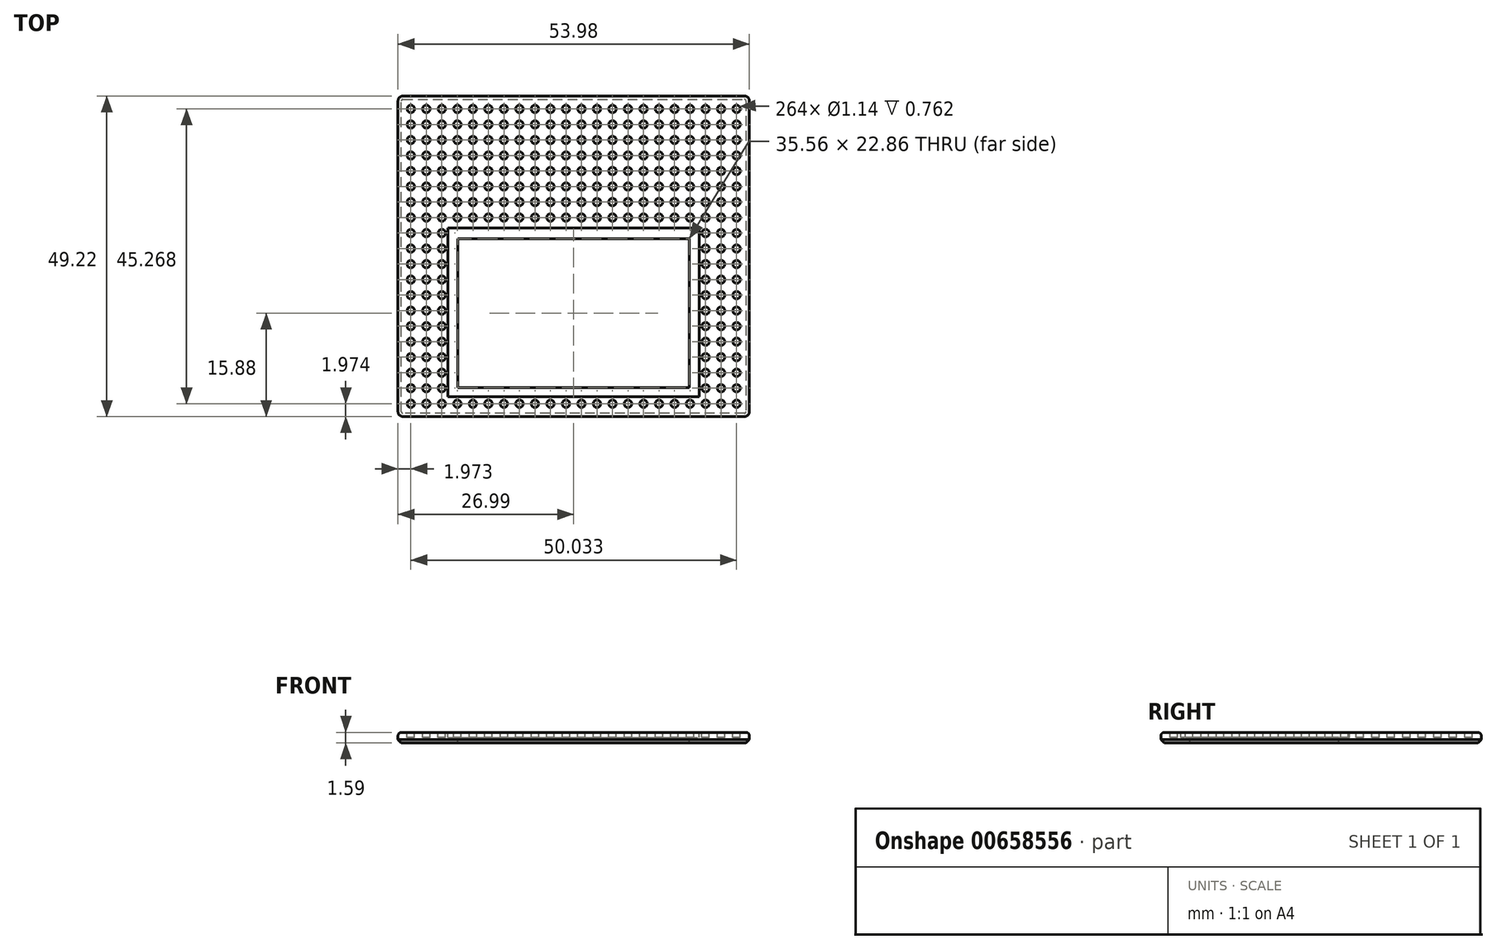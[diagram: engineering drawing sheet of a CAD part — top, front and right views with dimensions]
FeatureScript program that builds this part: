
annotation { "Feature Type Name" : "Feature", "Feature Type Description" : "" }
export const myFeature = defineFeature(function(context is Context, id is Id, definition is map)
    precondition{}
    {
        {
            var Q0;
            Q0=qCreatedBy(makeId("Top.planeOp"),FACE);
            var sketch = newSketch(context, id + "F0", { "sketchPlane" : qUnion([Q0])});
            skLineSegment(sketch, "E0.bottom", {"start": v(-26.99, 33.34) * mm, "end": v(26.99, 33.34) * mm});
            skLineSegment(sketch, "E0.top", {"start": v(-26.99, -15.88) * mm, "end": v(26.99, -15.88) * mm});
            skLineSegment(sketch, "E0.left", {"start": v(-26.99, 33.34) * mm, "end": v(-26.99, -15.88) * mm});
            skLineSegment(sketch, "E0.right", {"start": v(26.99, 33.34) * mm, "end": v(26.99, -15.87) * mm});
            skSolve(sketch);
        }
        {
            var Q0;
            Q0=qSketchRegion(id+"F0",true);
            extrude(context, id + "F1", {"entities" : qUnion([Q0]), "depth" : 1.59 * mm, "offsetDistance" : 25.4 * mm});
        }
        {
            var Q0;
            Q0=makeQuery(id+"F1.opExtrude","CAP_FACE",FACE,{"disambiguationData":[OSD([sQuery(id+"F0.wireOp",EDGE,"E0.bottom"),sQuery(id+"F0.wireOp",EDGE,"E0.top"),sQuery(id+"F0.wireOp",EDGE,"E0.left"),sQuery(id+"F0.wireOp",EDGE,"E0.right")])],"isStart":false});
            var sketch = newSketch(context, id + "F2", { "sketchPlane" : qUnion([Q0])});
            skCircle(sketch, "E1", {"center": v(-25.02, -13.9) * mm, "radius": 0.57 * mm});
            skCircle(sketch, "E2.0.1.0", {"center": v(-25.02, -11.52) * mm, "radius": 0.57 * mm});
            skCircle(sketch, "E2.0.2.0", {"center": v(-25.02, -9.14) * mm, "radius": 0.57 * mm});
            skCircle(sketch, "E2.0.3.0", {"center": v(-25.02, -6.76) * mm, "radius": 0.57 * mm});
            skCircle(sketch, "E2.0.4.0", {"center": v(-25.02, -4.38) * mm, "radius": 0.57 * mm});
            skCircle(sketch, "E2.0.5.0", {"center": v(-25.02, -2) * mm, "radius": 0.57 * mm});
            skCircle(sketch, "E2.0.6.0", {"center": v(-25.02, 0.39) * mm, "radius": 0.57 * mm});
            skCircle(sketch, "E2.0.7.0", {"center": v(-25.02, 2.77) * mm, "radius": 0.57 * mm});
            skCircle(sketch, "E2.0.8.0", {"center": v(-25.02, 5.15) * mm, "radius": 0.57 * mm});
            skCircle(sketch, "E2.0.9.0", {"center": v(-25.02, 7.54) * mm, "radius": 0.57 * mm});
            skCircle(sketch, "E2.0.10.0", {"center": v(-25.02, 9.92) * mm, "radius": 0.57 * mm});
            skCircle(sketch, "E2.0.11.0", {"center": v(-25.02, 12.3) * mm, "radius": 0.57 * mm});
            skCircle(sketch, "E2.1.0.0", {"center": v(-22.63, -13.9) * mm, "radius": 0.57 * mm});
            skCircle(sketch, "E2.1.1.0", {"center": v(-22.63, -11.52) * mm, "radius": 0.57 * mm});
            skCircle(sketch, "E2.1.2.0", {"center": v(-22.63, -9.14) * mm, "radius": 0.57 * mm});
            skCircle(sketch, "E2.1.3.0", {"center": v(-22.63, -6.76) * mm, "radius": 0.57 * mm});
            skCircle(sketch, "E2.1.4.0", {"center": v(-22.63, -4.38) * mm, "radius": 0.57 * mm});
            skCircle(sketch, "E2.1.5.0", {"center": v(-22.63, -2) * mm, "radius": 0.57 * mm});
            skCircle(sketch, "E2.1.6.0", {"center": v(-22.63, 0.39) * mm, "radius": 0.57 * mm});
            skCircle(sketch, "E2.1.7.0", {"center": v(-22.63, 2.77) * mm, "radius": 0.57 * mm});
            skCircle(sketch, "E2.1.8.0", {"center": v(-22.63, 5.15) * mm, "radius": 0.57 * mm});
            skCircle(sketch, "E2.1.9.0", {"center": v(-22.63, 7.54) * mm, "radius": 0.57 * mm});
            skCircle(sketch, "E2.1.10.0", {"center": v(-22.63, 9.92) * mm, "radius": 0.57 * mm});
            skCircle(sketch, "E2.1.11.0", {"center": v(-22.63, 12.3) * mm, "radius": 0.57 * mm});
            skCircle(sketch, "E2.2.0.0", {"center": v(-20.25, -13.9) * mm, "radius": 0.57 * mm});
            skCircle(sketch, "E2.2.1.0", {"center": v(-20.25, -11.52) * mm, "radius": 0.57 * mm});
            skCircle(sketch, "E2.2.2.0", {"center": v(-20.25, -9.14) * mm, "radius": 0.57 * mm});
            skCircle(sketch, "E2.2.3.0", {"center": v(-20.25, -6.76) * mm, "radius": 0.57 * mm});
            skCircle(sketch, "E2.2.4.0", {"center": v(-20.25, -4.38) * mm, "radius": 0.57 * mm});
            skCircle(sketch, "E2.2.5.0", {"center": v(-20.25, -2) * mm, "radius": 0.57 * mm});
            skCircle(sketch, "E2.2.6.0", {"center": v(-20.25, 0.39) * mm, "radius": 0.57 * mm});
            skCircle(sketch, "E2.2.7.0", {"center": v(-20.25, 2.77) * mm, "radius": 0.57 * mm});
            skCircle(sketch, "E2.2.8.0", {"center": v(-20.25, 5.15) * mm, "radius": 0.57 * mm});
            skCircle(sketch, "E2.2.9.0", {"center": v(-20.25, 7.54) * mm, "radius": 0.57 * mm});
            skCircle(sketch, "E2.2.10.0", {"center": v(-20.25, 9.92) * mm, "radius": 0.57 * mm});
            skCircle(sketch, "E2.2.11.0", {"center": v(-20.25, 12.3) * mm, "radius": 0.57 * mm});
            skCircle(sketch, "E2.3.0.0", {"center": v(-17.87, -13.9) * mm, "radius": 0.57 * mm});
            skCircle(sketch, "E2.3.1.0", {"center": v(-17.87, -11.52) * mm, "radius": 0.57 * mm});
            skCircle(sketch, "E2.3.2.0", {"center": v(-17.87, -9.14) * mm, "radius": 0.57 * mm});
            skCircle(sketch, "E2.3.3.0", {"center": v(-17.87, -6.76) * mm, "radius": 0.57 * mm});
            skCircle(sketch, "E2.3.4.0", {"center": v(-17.87, -4.38) * mm, "radius": 0.57 * mm});
            skCircle(sketch, "E2.3.5.0", {"center": v(-17.87, -2) * mm, "radius": 0.57 * mm});
            skCircle(sketch, "E2.3.6.0", {"center": v(-17.87, 0.39) * mm, "radius": 0.57 * mm});
            skCircle(sketch, "E2.3.7.0", {"center": v(-17.87, 2.77) * mm, "radius": 0.57 * mm});
            skCircle(sketch, "E2.3.8.0", {"center": v(-17.87, 5.15) * mm, "radius": 0.57 * mm});
            skCircle(sketch, "E2.3.9.0", {"center": v(-17.87, 7.54) * mm, "radius": 0.57 * mm});
            skCircle(sketch, "E2.3.10.0", {"center": v(-17.87, 9.92) * mm, "radius": 0.57 * mm});
            skCircle(sketch, "E2.3.11.0", {"center": v(-17.87, 12.3) * mm, "radius": 0.57 * mm});
            skCircle(sketch, "E2.4.0.0", {"center": v(-15.49, -13.9) * mm, "radius": 0.57 * mm});
            skCircle(sketch, "E2.4.1.0", {"center": v(-15.49, -11.52) * mm, "radius": 0.57 * mm});
            skCircle(sketch, "E2.4.2.0", {"center": v(-15.49, -9.14) * mm, "radius": 0.57 * mm});
            skCircle(sketch, "E2.4.3.0", {"center": v(-15.49, -6.76) * mm, "radius": 0.57 * mm});
            skCircle(sketch, "E2.4.4.0", {"center": v(-15.49, -4.38) * mm, "radius": 0.57 * mm});
            skCircle(sketch, "E2.4.5.0", {"center": v(-15.49, -2) * mm, "radius": 0.57 * mm});
            skCircle(sketch, "E2.4.6.0", {"center": v(-15.49, 0.39) * mm, "radius": 0.57 * mm});
            skCircle(sketch, "E2.4.7.0", {"center": v(-15.49, 2.77) * mm, "radius": 0.57 * mm});
            skCircle(sketch, "E2.4.8.0", {"center": v(-15.49, 5.15) * mm, "radius": 0.57 * mm});
            skCircle(sketch, "E2.4.9.0", {"center": v(-15.49, 7.54) * mm, "radius": 0.57 * mm});
            skCircle(sketch, "E2.4.10.0", {"center": v(-15.49, 9.92) * mm, "radius": 0.57 * mm});
            skCircle(sketch, "E2.4.11.0", {"center": v(-15.49, 12.3) * mm, "radius": 0.57 * mm});
            skCircle(sketch, "E2.5.0.0", {"center": v(-13.1, -13.9) * mm, "radius": 0.57 * mm});
            skCircle(sketch, "E2.5.1.0", {"center": v(-13.1, -11.52) * mm, "radius": 0.57 * mm});
            skCircle(sketch, "E2.5.2.0", {"center": v(-13.1, -9.14) * mm, "radius": 0.57 * mm});
            skCircle(sketch, "E2.5.3.0", {"center": v(-13.1, -6.76) * mm, "radius": 0.57 * mm});
            skCircle(sketch, "E2.5.4.0", {"center": v(-13.1, -4.38) * mm, "radius": 0.57 * mm});
            skCircle(sketch, "E2.5.5.0", {"center": v(-13.1, -2) * mm, "radius": 0.57 * mm});
            skCircle(sketch, "E2.5.6.0", {"center": v(-13.1, 0.39) * mm, "radius": 0.57 * mm});
            skCircle(sketch, "E2.5.7.0", {"center": v(-13.1, 2.77) * mm, "radius": 0.57 * mm});
            skCircle(sketch, "E2.5.8.0", {"center": v(-13.1, 5.15) * mm, "radius": 0.57 * mm});
            skCircle(sketch, "E2.5.9.0", {"center": v(-13.1, 7.54) * mm, "radius": 0.57 * mm});
            skCircle(sketch, "E2.5.10.0", {"center": v(-13.1, 9.92) * mm, "radius": 0.57 * mm});
            skCircle(sketch, "E2.5.11.0", {"center": v(-13.1, 12.3) * mm, "radius": 0.57 * mm});
            skCircle(sketch, "E2.6.0.0", {"center": v(-10.72, -13.9) * mm, "radius": 0.57 * mm});
            skCircle(sketch, "E2.6.1.0", {"center": v(-10.72, -11.52) * mm, "radius": 0.57 * mm});
            skCircle(sketch, "E2.6.2.0", {"center": v(-10.72, -9.14) * mm, "radius": 0.57 * mm});
            skCircle(sketch, "E2.6.3.0", {"center": v(-10.72, -6.76) * mm, "radius": 0.57 * mm});
            skCircle(sketch, "E2.6.4.0", {"center": v(-10.72, -4.38) * mm, "radius": 0.57 * mm});
            skCircle(sketch, "E2.6.5.0", {"center": v(-10.72, -2) * mm, "radius": 0.57 * mm});
            skCircle(sketch, "E2.6.6.0", {"center": v(-10.72, 0.39) * mm, "radius": 0.57 * mm});
            skCircle(sketch, "E2.6.7.0", {"center": v(-10.72, 2.77) * mm, "radius": 0.57 * mm});
            skCircle(sketch, "E2.6.8.0", {"center": v(-10.72, 5.15) * mm, "radius": 0.57 * mm});
            skCircle(sketch, "E2.6.9.0", {"center": v(-10.72, 7.54) * mm, "radius": 0.57 * mm});
            skCircle(sketch, "E2.6.10.0", {"center": v(-10.72, 9.92) * mm, "radius": 0.57 * mm});
            skCircle(sketch, "E2.6.11.0", {"center": v(-10.72, 12.3) * mm, "radius": 0.57 * mm});
            skCircle(sketch, "E2.7.0.0", {"center": v(-8.34, -13.9) * mm, "radius": 0.57 * mm});
            skCircle(sketch, "E2.7.1.0", {"center": v(-8.34, -11.52) * mm, "radius": 0.57 * mm});
            skCircle(sketch, "E2.7.2.0", {"center": v(-8.34, -9.14) * mm, "radius": 0.57 * mm});
            skCircle(sketch, "E2.7.3.0", {"center": v(-8.34, -6.76) * mm, "radius": 0.57 * mm});
            skCircle(sketch, "E2.7.4.0", {"center": v(-8.34, -4.38) * mm, "radius": 0.57 * mm});
            skCircle(sketch, "E2.7.5.0", {"center": v(-8.34, -2) * mm, "radius": 0.57 * mm});
            skCircle(sketch, "E2.7.6.0", {"center": v(-8.34, 0.39) * mm, "radius": 0.57 * mm});
            skCircle(sketch, "E2.7.7.0", {"center": v(-8.34, 2.77) * mm, "radius": 0.57 * mm});
            skCircle(sketch, "E2.7.8.0", {"center": v(-8.34, 5.15) * mm, "radius": 0.57 * mm});
            skCircle(sketch, "E2.7.9.0", {"center": v(-8.34, 7.54) * mm, "radius": 0.57 * mm});
            skCircle(sketch, "E2.7.10.0", {"center": v(-8.34, 9.92) * mm, "radius": 0.57 * mm});
            skCircle(sketch, "E2.7.11.0", {"center": v(-8.34, 12.3) * mm, "radius": 0.57 * mm});
            skCircle(sketch, "E2.8.0.0", {"center": v(-5.96, -13.9) * mm, "radius": 0.57 * mm});
            skCircle(sketch, "E2.8.1.0", {"center": v(-5.96, -11.52) * mm, "radius": 0.57 * mm});
            skCircle(sketch, "E2.8.2.0", {"center": v(-5.96, -9.14) * mm, "radius": 0.57 * mm});
            skCircle(sketch, "E2.8.3.0", {"center": v(-5.96, -6.76) * mm, "radius": 0.57 * mm});
            skCircle(sketch, "E2.8.4.0", {"center": v(-5.96, -4.38) * mm, "radius": 0.57 * mm});
            skCircle(sketch, "E2.8.5.0", {"center": v(-5.96, -2) * mm, "radius": 0.57 * mm});
            skCircle(sketch, "E2.8.6.0", {"center": v(-5.96, 0.39) * mm, "radius": 0.57 * mm});
            skCircle(sketch, "E2.8.7.0", {"center": v(-5.96, 2.77) * mm, "radius": 0.57 * mm});
            skCircle(sketch, "E2.8.8.0", {"center": v(-5.96, 5.15) * mm, "radius": 0.57 * mm});
            skCircle(sketch, "E2.8.9.0", {"center": v(-5.96, 7.54) * mm, "radius": 0.57 * mm});
            skCircle(sketch, "E2.8.10.0", {"center": v(-5.96, 9.92) * mm, "radius": 0.57 * mm});
            skCircle(sketch, "E2.8.11.0", {"center": v(-5.96, 12.3) * mm, "radius": 0.57 * mm});
            skCircle(sketch, "E2.9.0.0", {"center": v(-3.57, -13.9) * mm, "radius": 0.57 * mm});
            skCircle(sketch, "E2.9.1.0", {"center": v(-3.57, -11.52) * mm, "radius": 0.57 * mm});
            skCircle(sketch, "E2.9.2.0", {"center": v(-3.57, -9.14) * mm, "radius": 0.57 * mm});
            skCircle(sketch, "E2.9.3.0", {"center": v(-3.57, -6.76) * mm, "radius": 0.57 * mm});
            skCircle(sketch, "E2.9.4.0", {"center": v(-3.57, -4.38) * mm, "radius": 0.57 * mm});
            skCircle(sketch, "E2.9.5.0", {"center": v(-3.57, -2) * mm, "radius": 0.57 * mm});
            skCircle(sketch, "E2.9.6.0", {"center": v(-3.57, 0.39) * mm, "radius": 0.57 * mm});
            skCircle(sketch, "E2.9.7.0", {"center": v(-3.57, 2.77) * mm, "radius": 0.57 * mm});
            skCircle(sketch, "E2.9.8.0", {"center": v(-3.57, 5.15) * mm, "radius": 0.57 * mm});
            skCircle(sketch, "E2.9.9.0", {"center": v(-3.57, 7.54) * mm, "radius": 0.57 * mm});
            skCircle(sketch, "E2.9.10.0", {"center": v(-3.57, 9.92) * mm, "radius": 0.57 * mm});
            skCircle(sketch, "E2.9.11.0", {"center": v(-3.57, 12.3) * mm, "radius": 0.57 * mm});
            skCircle(sketch, "E2.10.0.0", {"center": v(-1.2, -13.9) * mm, "radius": 0.57 * mm});
            skCircle(sketch, "E2.10.1.0", {"center": v(-1.2, -11.52) * mm, "radius": 0.57 * mm});
            skCircle(sketch, "E2.10.2.0", {"center": v(-1.2, -9.14) * mm, "radius": 0.57 * mm});
            skCircle(sketch, "E2.10.3.0", {"center": v(-1.2, -6.76) * mm, "radius": 0.57 * mm});
            skCircle(sketch, "E2.10.4.0", {"center": v(-1.2, -4.38) * mm, "radius": 0.57 * mm});
            skCircle(sketch, "E2.10.5.0", {"center": v(-1.2, -2) * mm, "radius": 0.57 * mm});
            skCircle(sketch, "E2.10.6.0", {"center": v(-1.2, 0.39) * mm, "radius": 0.57 * mm});
            skCircle(sketch, "E2.10.7.0", {"center": v(-1.2, 2.77) * mm, "radius": 0.57 * mm});
            skCircle(sketch, "E2.10.8.0", {"center": v(-1.2, 5.15) * mm, "radius": 0.57 * mm});
            skCircle(sketch, "E2.10.9.0", {"center": v(-1.2, 7.54) * mm, "radius": 0.57 * mm});
            skCircle(sketch, "E2.10.10.0", {"center": v(-1.2, 9.92) * mm, "radius": 0.57 * mm});
            skCircle(sketch, "E2.10.11.0", {"center": v(-1.2, 12.3) * mm, "radius": 0.57 * mm});
            skCircle(sketch, "E2.11.0.0", {"center": v(1.2, -13.9) * mm, "radius": 0.57 * mm});
            skCircle(sketch, "E2.11.1.0", {"center": v(1.2, -11.52) * mm, "radius": 0.57 * mm});
            skCircle(sketch, "E2.11.2.0", {"center": v(1.2, -9.14) * mm, "radius": 0.57 * mm});
            skCircle(sketch, "E2.11.3.0", {"center": v(1.2, -6.76) * mm, "radius": 0.57 * mm});
            skCircle(sketch, "E2.11.4.0", {"center": v(1.2, -4.38) * mm, "radius": 0.57 * mm});
            skCircle(sketch, "E2.11.5.0", {"center": v(1.2, -2) * mm, "radius": 0.57 * mm});
            skCircle(sketch, "E2.11.6.0", {"center": v(1.2, 0.39) * mm, "radius": 0.57 * mm});
            skCircle(sketch, "E2.11.7.0", {"center": v(1.2, 2.77) * mm, "radius": 0.57 * mm});
            skCircle(sketch, "E2.11.8.0", {"center": v(1.2, 5.15) * mm, "radius": 0.57 * mm});
            skCircle(sketch, "E2.11.9.0", {"center": v(1.2, 7.54) * mm, "radius": 0.57 * mm});
            skCircle(sketch, "E2.11.10.0", {"center": v(1.2, 9.92) * mm, "radius": 0.57 * mm});
            skCircle(sketch, "E2.11.11.0", {"center": v(1.2, 12.3) * mm, "radius": 0.57 * mm});
            skCircle(sketch, "E2.12.0.0", {"center": v(3.57, -13.9) * mm, "radius": 0.57 * mm});
            skCircle(sketch, "E2.12.1.0", {"center": v(3.57, -11.52) * mm, "radius": 0.57 * mm});
            skCircle(sketch, "E2.12.2.0", {"center": v(3.57, -9.14) * mm, "radius": 0.57 * mm});
            skCircle(sketch, "E2.12.3.0", {"center": v(3.57, -6.76) * mm, "radius": 0.57 * mm});
            skCircle(sketch, "E2.12.4.0", {"center": v(3.57, -4.38) * mm, "radius": 0.57 * mm});
            skCircle(sketch, "E2.12.5.0", {"center": v(3.57, -2) * mm, "radius": 0.57 * mm});
            skCircle(sketch, "E2.12.6.0", {"center": v(3.57, 0.39) * mm, "radius": 0.57 * mm});
            skCircle(sketch, "E2.12.7.0", {"center": v(3.57, 2.77) * mm, "radius": 0.57 * mm});
            skCircle(sketch, "E2.12.8.0", {"center": v(3.57, 5.15) * mm, "radius": 0.57 * mm});
            skCircle(sketch, "E2.12.9.0", {"center": v(3.57, 7.54) * mm, "radius": 0.57 * mm});
            skCircle(sketch, "E2.12.10.0", {"center": v(3.57, 9.92) * mm, "radius": 0.57 * mm});
            skCircle(sketch, "E2.12.11.0", {"center": v(3.57, 12.3) * mm, "radius": 0.57 * mm});
            skCircle(sketch, "E2.13.0.0", {"center": v(5.96, -13.9) * mm, "radius": 0.57 * mm});
            skCircle(sketch, "E2.13.1.0", {"center": v(5.96, -11.52) * mm, "radius": 0.57 * mm});
            skCircle(sketch, "E2.13.2.0", {"center": v(5.96, -9.14) * mm, "radius": 0.57 * mm});
            skCircle(sketch, "E2.13.3.0", {"center": v(5.96, -6.76) * mm, "radius": 0.57 * mm});
            skCircle(sketch, "E2.13.4.0", {"center": v(5.96, -4.38) * mm, "radius": 0.57 * mm});
            skCircle(sketch, "E2.13.5.0", {"center": v(5.96, -2) * mm, "radius": 0.57 * mm});
            skCircle(sketch, "E2.13.6.0", {"center": v(5.96, 0.39) * mm, "radius": 0.57 * mm});
            skCircle(sketch, "E2.13.7.0", {"center": v(5.96, 2.77) * mm, "radius": 0.57 * mm});
            skCircle(sketch, "E2.13.8.0", {"center": v(5.96, 5.15) * mm, "radius": 0.57 * mm});
            skCircle(sketch, "E2.13.9.0", {"center": v(5.96, 7.54) * mm, "radius": 0.57 * mm});
            skCircle(sketch, "E2.13.10.0", {"center": v(5.96, 9.92) * mm, "radius": 0.57 * mm});
            skCircle(sketch, "E2.13.11.0", {"center": v(5.96, 12.3) * mm, "radius": 0.57 * mm});
            skCircle(sketch, "E2.14.0.0", {"center": v(8.34, -13.9) * mm, "radius": 0.57 * mm});
            skCircle(sketch, "E2.14.1.0", {"center": v(8.34, -11.52) * mm, "radius": 0.57 * mm});
            skCircle(sketch, "E2.14.2.0", {"center": v(8.34, -9.14) * mm, "radius": 0.57 * mm});
            skCircle(sketch, "E2.14.3.0", {"center": v(8.34, -6.76) * mm, "radius": 0.57 * mm});
            skCircle(sketch, "E2.14.4.0", {"center": v(8.34, -4.38) * mm, "radius": 0.57 * mm});
            skCircle(sketch, "E2.14.5.0", {"center": v(8.34, -2) * mm, "radius": 0.57 * mm});
            skCircle(sketch, "E2.14.6.0", {"center": v(8.34, 0.39) * mm, "radius": 0.57 * mm});
            skCircle(sketch, "E2.14.7.0", {"center": v(8.34, 2.77) * mm, "radius": 0.57 * mm});
            skCircle(sketch, "E2.14.8.0", {"center": v(8.34, 5.15) * mm, "radius": 0.57 * mm});
            skCircle(sketch, "E2.14.9.0", {"center": v(8.34, 7.54) * mm, "radius": 0.57 * mm});
            skCircle(sketch, "E2.14.10.0", {"center": v(8.34, 9.92) * mm, "radius": 0.57 * mm});
            skCircle(sketch, "E2.14.11.0", {"center": v(8.34, 12.3) * mm, "radius": 0.57 * mm});
            skCircle(sketch, "E2.15.0.0", {"center": v(10.72, -13.9) * mm, "radius": 0.57 * mm});
            skCircle(sketch, "E2.15.1.0", {"center": v(10.72, -11.52) * mm, "radius": 0.57 * mm});
            skCircle(sketch, "E2.15.2.0", {"center": v(10.72, -9.14) * mm, "radius": 0.57 * mm});
            skCircle(sketch, "E2.15.3.0", {"center": v(10.72, -6.76) * mm, "radius": 0.57 * mm});
            skCircle(sketch, "E2.15.4.0", {"center": v(10.72, -4.38) * mm, "radius": 0.57 * mm});
            skCircle(sketch, "E2.15.5.0", {"center": v(10.72, -2) * mm, "radius": 0.57 * mm});
            skCircle(sketch, "E2.15.6.0", {"center": v(10.72, 0.39) * mm, "radius": 0.57 * mm});
            skCircle(sketch, "E2.15.7.0", {"center": v(10.72, 2.77) * mm, "radius": 0.57 * mm});
            skCircle(sketch, "E2.15.8.0", {"center": v(10.72, 5.15) * mm, "radius": 0.57 * mm});
            skCircle(sketch, "E2.15.9.0", {"center": v(10.72, 7.54) * mm, "radius": 0.57 * mm});
            skCircle(sketch, "E2.15.10.0", {"center": v(10.72, 9.92) * mm, "radius": 0.57 * mm});
            skCircle(sketch, "E2.15.11.0", {"center": v(10.72, 12.3) * mm, "radius": 0.57 * mm});
            skCircle(sketch, "E2.16.0.0", {"center": v(13.1, -13.9) * mm, "radius": 0.57 * mm});
            skCircle(sketch, "E2.16.1.0", {"center": v(13.1, -11.52) * mm, "radius": 0.57 * mm});
            skCircle(sketch, "E2.16.2.0", {"center": v(13.1, -9.14) * mm, "radius": 0.57 * mm});
            skCircle(sketch, "E2.16.3.0", {"center": v(13.1, -6.76) * mm, "radius": 0.57 * mm});
            skCircle(sketch, "E2.16.4.0", {"center": v(13.1, -4.38) * mm, "radius": 0.57 * mm});
            skCircle(sketch, "E2.16.5.0", {"center": v(13.1, -2) * mm, "radius": 0.57 * mm});
            skCircle(sketch, "E2.16.6.0", {"center": v(13.1, 0.39) * mm, "radius": 0.57 * mm});
            skCircle(sketch, "E2.16.7.0", {"center": v(13.1, 2.77) * mm, "radius": 0.57 * mm});
            skCircle(sketch, "E2.16.8.0", {"center": v(13.1, 5.15) * mm, "radius": 0.57 * mm});
            skCircle(sketch, "E2.16.9.0", {"center": v(13.1, 7.54) * mm, "radius": 0.57 * mm});
            skCircle(sketch, "E2.16.10.0", {"center": v(13.1, 9.92) * mm, "radius": 0.57 * mm});
            skCircle(sketch, "E2.16.11.0", {"center": v(13.1, 12.3) * mm, "radius": 0.57 * mm});
            skCircle(sketch, "E2.17.0.0", {"center": v(15.49, -13.9) * mm, "radius": 0.57 * mm});
            skCircle(sketch, "E2.17.1.0", {"center": v(15.49, -11.52) * mm, "radius": 0.57 * mm});
            skCircle(sketch, "E2.17.2.0", {"center": v(15.49, -9.14) * mm, "radius": 0.57 * mm});
            skCircle(sketch, "E2.17.3.0", {"center": v(15.49, -6.76) * mm, "radius": 0.57 * mm});
            skCircle(sketch, "E2.17.4.0", {"center": v(15.49, -4.38) * mm, "radius": 0.57 * mm});
            skCircle(sketch, "E2.17.5.0", {"center": v(15.49, -2) * mm, "radius": 0.57 * mm});
            skCircle(sketch, "E2.17.6.0", {"center": v(15.49, 0.39) * mm, "radius": 0.57 * mm});
            skCircle(sketch, "E2.17.7.0", {"center": v(15.49, 2.77) * mm, "radius": 0.57 * mm});
            skCircle(sketch, "E2.17.8.0", {"center": v(15.49, 5.15) * mm, "radius": 0.57 * mm});
            skCircle(sketch, "E2.17.9.0", {"center": v(15.49, 7.54) * mm, "radius": 0.57 * mm});
            skCircle(sketch, "E2.17.10.0", {"center": v(15.49, 9.92) * mm, "radius": 0.57 * mm});
            skCircle(sketch, "E2.17.11.0", {"center": v(15.49, 12.3) * mm, "radius": 0.57 * mm});
            skCircle(sketch, "E2.18.0.0", {"center": v(17.87, -13.9) * mm, "radius": 0.57 * mm});
            skCircle(sketch, "E2.18.1.0", {"center": v(17.87, -11.52) * mm, "radius": 0.57 * mm});
            skCircle(sketch, "E2.18.2.0", {"center": v(17.87, -9.14) * mm, "radius": 0.57 * mm});
            skCircle(sketch, "E2.18.3.0", {"center": v(17.87, -6.76) * mm, "radius": 0.57 * mm});
            skCircle(sketch, "E2.18.4.0", {"center": v(17.87, -4.38) * mm, "radius": 0.57 * mm});
            skCircle(sketch, "E2.18.5.0", {"center": v(17.87, -2) * mm, "radius": 0.57 * mm});
            skCircle(sketch, "E2.18.6.0", {"center": v(17.87, 0.39) * mm, "radius": 0.57 * mm});
            skCircle(sketch, "E2.18.7.0", {"center": v(17.87, 2.77) * mm, "radius": 0.57 * mm});
            skCircle(sketch, "E2.18.8.0", {"center": v(17.87, 5.15) * mm, "radius": 0.57 * mm});
            skCircle(sketch, "E2.18.9.0", {"center": v(17.87, 7.54) * mm, "radius": 0.57 * mm});
            skCircle(sketch, "E2.18.10.0", {"center": v(17.87, 9.92) * mm, "radius": 0.57 * mm});
            skCircle(sketch, "E2.18.11.0", {"center": v(17.87, 12.3) * mm, "radius": 0.57 * mm});
            skCircle(sketch, "E2.19.0.0", {"center": v(20.25, -13.9) * mm, "radius": 0.57 * mm});
            skCircle(sketch, "E2.19.1.0", {"center": v(20.25, -11.52) * mm, "radius": 0.57 * mm});
            skCircle(sketch, "E2.19.2.0", {"center": v(20.25, -9.14) * mm, "radius": 0.57 * mm});
            skCircle(sketch, "E2.19.3.0", {"center": v(20.25, -6.76) * mm, "radius": 0.57 * mm});
            skCircle(sketch, "E2.19.4.0", {"center": v(20.25, -4.38) * mm, "radius": 0.57 * mm});
            skCircle(sketch, "E2.19.5.0", {"center": v(20.25, -2) * mm, "radius": 0.57 * mm});
            skCircle(sketch, "E2.19.6.0", {"center": v(20.25, 0.39) * mm, "radius": 0.57 * mm});
            skCircle(sketch, "E2.19.7.0", {"center": v(20.25, 2.77) * mm, "radius": 0.57 * mm});
            skCircle(sketch, "E2.19.8.0", {"center": v(20.25, 5.15) * mm, "radius": 0.57 * mm});
            skCircle(sketch, "E2.19.9.0", {"center": v(20.25, 7.54) * mm, "radius": 0.57 * mm});
            skCircle(sketch, "E2.19.10.0", {"center": v(20.25, 9.92) * mm, "radius": 0.57 * mm});
            skCircle(sketch, "E2.19.11.0", {"center": v(20.25, 12.3) * mm, "radius": 0.57 * mm});
            skCircle(sketch, "E2.20.0.0", {"center": v(22.63, -13.9) * mm, "radius": 0.57 * mm});
            skCircle(sketch, "E2.20.1.0", {"center": v(22.63, -11.52) * mm, "radius": 0.57 * mm});
            skCircle(sketch, "E2.20.2.0", {"center": v(22.63, -9.14) * mm, "radius": 0.57 * mm});
            skCircle(sketch, "E2.20.3.0", {"center": v(22.63, -6.76) * mm, "radius": 0.57 * mm});
            skCircle(sketch, "E2.20.4.0", {"center": v(22.63, -4.38) * mm, "radius": 0.57 * mm});
            skCircle(sketch, "E2.20.5.0", {"center": v(22.63, -2) * mm, "radius": 0.57 * mm});
            skCircle(sketch, "E2.20.6.0", {"center": v(22.63, 0.39) * mm, "radius": 0.57 * mm});
            skCircle(sketch, "E2.20.7.0", {"center": v(22.63, 2.77) * mm, "radius": 0.57 * mm});
            skCircle(sketch, "E2.20.8.0", {"center": v(22.63, 5.15) * mm, "radius": 0.57 * mm});
            skCircle(sketch, "E2.20.9.0", {"center": v(22.63, 7.54) * mm, "radius": 0.57 * mm});
            skCircle(sketch, "E2.20.10.0", {"center": v(22.63, 9.92) * mm, "radius": 0.57 * mm});
            skCircle(sketch, "E2.20.11.0", {"center": v(22.63, 12.3) * mm, "radius": 0.57 * mm});
            skCircle(sketch, "E2.21.0.0", {"center": v(25.02, -13.9) * mm, "radius": 0.57 * mm});
            skCircle(sketch, "E2.21.1.0", {"center": v(25.02, -11.52) * mm, "radius": 0.57 * mm});
            skCircle(sketch, "E2.21.2.0", {"center": v(25.02, -9.14) * mm, "radius": 0.57 * mm});
            skCircle(sketch, "E2.21.3.0", {"center": v(25.02, -6.76) * mm, "radius": 0.57 * mm});
            skCircle(sketch, "E2.21.4.0", {"center": v(25.02, -4.38) * mm, "radius": 0.57 * mm});
            skCircle(sketch, "E2.21.5.0", {"center": v(25.02, -2) * mm, "radius": 0.57 * mm});
            skCircle(sketch, "E2.21.6.0", {"center": v(25.02, 0.39) * mm, "radius": 0.57 * mm});
            skCircle(sketch, "E2.21.7.0", {"center": v(25.02, 2.77) * mm, "radius": 0.57 * mm});
            skCircle(sketch, "E2.21.8.0", {"center": v(25.02, 5.15) * mm, "radius": 0.57 * mm});
            skCircle(sketch, "E2.21.9.0", {"center": v(25.02, 7.54) * mm, "radius": 0.57 * mm});
            skCircle(sketch, "E2.21.10.0", {"center": v(25.02, 9.92) * mm, "radius": 0.57 * mm});
            skCircle(sketch, "E2.21.11.0", {"center": v(25.02, 12.3) * mm, "radius": 0.57 * mm});
            skLineSegment(sketch, "E2.direction1", {"start": v(-25.02, -13.9) * mm, "end": v(-22.63, -13.9) * mm, "construction": true});
            skLineSegment(sketch, "E2.direction2", {"start": v(-25.02, -13.9) * mm, "end": v(-25.02, -11.52) * mm, "construction": true});
            skCircle(sketch, "E3.0.0.12", {"center": v(-25.02, 14.68) * mm, "radius": 0.57 * mm});
            skCircle(sketch, "E3.0.0.13", {"center": v(-25.02, 17.07) * mm, "radius": 0.57 * mm});
            skCircle(sketch, "E3.0.0.14", {"center": v(-25.02, 19.45) * mm, "radius": 0.57 * mm});
            skCircle(sketch, "E3.0.0.15", {"center": v(-25.02, 21.83) * mm, "radius": 0.57 * mm});
            skCircle(sketch, "E3.0.0.16", {"center": v(-25.02, 24.21) * mm, "radius": 0.57 * mm});
            skCircle(sketch, "E3.0.0.17", {"center": v(-25.02, 26.6) * mm, "radius": 0.57 * mm});
            skCircle(sketch, "E3.0.1.12", {"center": v(-22.63, 14.68) * mm, "radius": 0.57 * mm});
            skCircle(sketch, "E3.0.1.13", {"center": v(-22.63, 17.07) * mm, "radius": 0.57 * mm});
            skCircle(sketch, "E3.0.1.14", {"center": v(-22.63, 19.45) * mm, "radius": 0.57 * mm});
            skCircle(sketch, "E3.0.1.15", {"center": v(-22.63, 21.83) * mm, "radius": 0.57 * mm});
            skCircle(sketch, "E3.0.1.16", {"center": v(-22.63, 24.21) * mm, "radius": 0.57 * mm});
            skCircle(sketch, "E3.0.1.17", {"center": v(-22.63, 26.6) * mm, "radius": 0.57 * mm});
            skCircle(sketch, "E3.0.2.12", {"center": v(-20.25, 14.68) * mm, "radius": 0.57 * mm});
            skCircle(sketch, "E3.0.2.13", {"center": v(-20.25, 17.07) * mm, "radius": 0.57 * mm});
            skCircle(sketch, "E3.0.2.14", {"center": v(-20.25, 19.45) * mm, "radius": 0.57 * mm});
            skCircle(sketch, "E3.0.2.15", {"center": v(-20.25, 21.83) * mm, "radius": 0.57 * mm});
            skCircle(sketch, "E3.0.2.16", {"center": v(-20.25, 24.21) * mm, "radius": 0.57 * mm});
            skCircle(sketch, "E3.0.2.17", {"center": v(-20.25, 26.6) * mm, "radius": 0.57 * mm});
            skCircle(sketch, "E3.0.3.12", {"center": v(-17.87, 14.68) * mm, "radius": 0.57 * mm});
            skCircle(sketch, "E3.0.3.13", {"center": v(-17.87, 17.07) * mm, "radius": 0.57 * mm});
            skCircle(sketch, "E3.0.3.14", {"center": v(-17.87, 19.45) * mm, "radius": 0.57 * mm});
            skCircle(sketch, "E3.0.3.15", {"center": v(-17.87, 21.83) * mm, "radius": 0.57 * mm});
            skCircle(sketch, "E3.0.3.16", {"center": v(-17.87, 24.21) * mm, "radius": 0.57 * mm});
            skCircle(sketch, "E3.0.3.17", {"center": v(-17.87, 26.6) * mm, "radius": 0.57 * mm});
            skCircle(sketch, "E3.0.4.12", {"center": v(-15.49, 14.68) * mm, "radius": 0.57 * mm});
            skCircle(sketch, "E3.0.4.13", {"center": v(-15.49, 17.07) * mm, "radius": 0.57 * mm});
            skCircle(sketch, "E3.0.4.14", {"center": v(-15.49, 19.45) * mm, "radius": 0.57 * mm});
            skCircle(sketch, "E3.0.4.15", {"center": v(-15.49, 21.83) * mm, "radius": 0.57 * mm});
            skCircle(sketch, "E3.0.4.16", {"center": v(-15.49, 24.21) * mm, "radius": 0.57 * mm});
            skCircle(sketch, "E3.0.4.17", {"center": v(-15.49, 26.6) * mm, "radius": 0.57 * mm});
            skCircle(sketch, "E3.0.5.12", {"center": v(-13.1, 14.68) * mm, "radius": 0.57 * mm});
            skCircle(sketch, "E3.0.5.13", {"center": v(-13.1, 17.07) * mm, "radius": 0.57 * mm});
            skCircle(sketch, "E3.0.5.14", {"center": v(-13.1, 19.45) * mm, "radius": 0.57 * mm});
            skCircle(sketch, "E3.0.5.15", {"center": v(-13.1, 21.83) * mm, "radius": 0.57 * mm});
            skCircle(sketch, "E3.0.5.16", {"center": v(-13.1, 24.21) * mm, "radius": 0.57 * mm});
            skCircle(sketch, "E3.0.5.17", {"center": v(-13.1, 26.6) * mm, "radius": 0.57 * mm});
            skCircle(sketch, "E3.0.6.12", {"center": v(-10.72, 14.68) * mm, "radius": 0.57 * mm});
            skCircle(sketch, "E3.0.6.13", {"center": v(-10.72, 17.07) * mm, "radius": 0.57 * mm});
            skCircle(sketch, "E3.0.6.14", {"center": v(-10.72, 19.45) * mm, "radius": 0.57 * mm});
            skCircle(sketch, "E3.0.6.15", {"center": v(-10.72, 21.83) * mm, "radius": 0.57 * mm});
            skCircle(sketch, "E3.0.6.16", {"center": v(-10.72, 24.21) * mm, "radius": 0.57 * mm});
            skCircle(sketch, "E3.0.6.17", {"center": v(-10.72, 26.6) * mm, "radius": 0.57 * mm});
            skCircle(sketch, "E3.0.7.12", {"center": v(-8.34, 14.68) * mm, "radius": 0.57 * mm});
            skCircle(sketch, "E3.0.7.13", {"center": v(-8.34, 17.07) * mm, "radius": 0.57 * mm});
            skCircle(sketch, "E3.0.7.14", {"center": v(-8.34, 19.45) * mm, "radius": 0.57 * mm});
            skCircle(sketch, "E3.0.7.15", {"center": v(-8.34, 21.83) * mm, "radius": 0.57 * mm});
            skCircle(sketch, "E3.0.7.16", {"center": v(-8.34, 24.21) * mm, "radius": 0.57 * mm});
            skCircle(sketch, "E3.0.7.17", {"center": v(-8.34, 26.6) * mm, "radius": 0.57 * mm});
            skCircle(sketch, "E3.0.8.12", {"center": v(-5.96, 14.68) * mm, "radius": 0.57 * mm});
            skCircle(sketch, "E3.0.8.13", {"center": v(-5.96, 17.07) * mm, "radius": 0.57 * mm});
            skCircle(sketch, "E3.0.8.14", {"center": v(-5.96, 19.45) * mm, "radius": 0.57 * mm});
            skCircle(sketch, "E3.0.8.15", {"center": v(-5.96, 21.83) * mm, "radius": 0.57 * mm});
            skCircle(sketch, "E3.0.8.16", {"center": v(-5.96, 24.21) * mm, "radius": 0.57 * mm});
            skCircle(sketch, "E3.0.8.17", {"center": v(-5.96, 26.6) * mm, "radius": 0.57 * mm});
            skCircle(sketch, "E3.0.9.12", {"center": v(-3.57, 14.68) * mm, "radius": 0.57 * mm});
            skCircle(sketch, "E3.0.9.13", {"center": v(-3.57, 17.07) * mm, "radius": 0.57 * mm});
            skCircle(sketch, "E3.0.9.14", {"center": v(-3.57, 19.45) * mm, "radius": 0.57 * mm});
            skCircle(sketch, "E3.0.9.15", {"center": v(-3.57, 21.83) * mm, "radius": 0.57 * mm});
            skCircle(sketch, "E3.0.9.16", {"center": v(-3.57, 24.21) * mm, "radius": 0.57 * mm});
            skCircle(sketch, "E3.0.9.17", {"center": v(-3.57, 26.6) * mm, "radius": 0.57 * mm});
            skCircle(sketch, "E3.0.10.12", {"center": v(-1.2, 14.68) * mm, "radius": 0.57 * mm});
            skCircle(sketch, "E3.0.10.13", {"center": v(-1.2, 17.07) * mm, "radius": 0.57 * mm});
            skCircle(sketch, "E3.0.10.14", {"center": v(-1.2, 19.45) * mm, "radius": 0.57 * mm});
            skCircle(sketch, "E3.0.10.15", {"center": v(-1.2, 21.83) * mm, "radius": 0.57 * mm});
            skCircle(sketch, "E3.0.10.16", {"center": v(-1.2, 24.21) * mm, "radius": 0.57 * mm});
            skCircle(sketch, "E3.0.10.17", {"center": v(-1.2, 26.6) * mm, "radius": 0.57 * mm});
            skCircle(sketch, "E3.0.11.12", {"center": v(1.2, 14.68) * mm, "radius": 0.57 * mm});
            skCircle(sketch, "E3.0.11.13", {"center": v(1.2, 17.07) * mm, "radius": 0.57 * mm});
            skCircle(sketch, "E3.0.11.14", {"center": v(1.2, 19.45) * mm, "radius": 0.57 * mm});
            skCircle(sketch, "E3.0.11.15", {"center": v(1.2, 21.83) * mm, "radius": 0.57 * mm});
            skCircle(sketch, "E3.0.11.16", {"center": v(1.2, 24.21) * mm, "radius": 0.57 * mm});
            skCircle(sketch, "E3.0.11.17", {"center": v(1.2, 26.6) * mm, "radius": 0.57 * mm});
            skCircle(sketch, "E3.0.12.12", {"center": v(3.57, 14.68) * mm, "radius": 0.57 * mm});
            skCircle(sketch, "E3.0.12.13", {"center": v(3.57, 17.07) * mm, "radius": 0.57 * mm});
            skCircle(sketch, "E3.0.12.14", {"center": v(3.57, 19.45) * mm, "radius": 0.57 * mm});
            skCircle(sketch, "E3.0.12.15", {"center": v(3.57, 21.83) * mm, "radius": 0.57 * mm});
            skCircle(sketch, "E3.0.12.16", {"center": v(3.57, 24.21) * mm, "radius": 0.57 * mm});
            skCircle(sketch, "E3.0.12.17", {"center": v(3.57, 26.6) * mm, "radius": 0.57 * mm});
            skCircle(sketch, "E3.0.13.12", {"center": v(5.96, 14.68) * mm, "radius": 0.57 * mm});
            skCircle(sketch, "E3.0.13.13", {"center": v(5.96, 17.07) * mm, "radius": 0.57 * mm});
            skCircle(sketch, "E3.0.13.14", {"center": v(5.96, 19.45) * mm, "radius": 0.57 * mm});
            skCircle(sketch, "E3.0.13.15", {"center": v(5.96, 21.83) * mm, "radius": 0.57 * mm});
            skCircle(sketch, "E3.0.13.16", {"center": v(5.96, 24.21) * mm, "radius": 0.57 * mm});
            skCircle(sketch, "E3.0.13.17", {"center": v(5.96, 26.6) * mm, "radius": 0.57 * mm});
            skCircle(sketch, "E3.0.14.12", {"center": v(8.34, 14.68) * mm, "radius": 0.57 * mm});
            skCircle(sketch, "E3.0.14.13", {"center": v(8.34, 17.07) * mm, "radius": 0.57 * mm});
            skCircle(sketch, "E3.0.14.14", {"center": v(8.34, 19.45) * mm, "radius": 0.57 * mm});
            skCircle(sketch, "E3.0.14.15", {"center": v(8.34, 21.83) * mm, "radius": 0.57 * mm});
            skCircle(sketch, "E3.0.14.16", {"center": v(8.34, 24.21) * mm, "radius": 0.57 * mm});
            skCircle(sketch, "E3.0.14.17", {"center": v(8.34, 26.6) * mm, "radius": 0.57 * mm});
            skCircle(sketch, "E3.0.15.12", {"center": v(10.72, 14.68) * mm, "radius": 0.57 * mm});
            skCircle(sketch, "E3.0.15.13", {"center": v(10.72, 17.07) * mm, "radius": 0.57 * mm});
            skCircle(sketch, "E3.0.15.14", {"center": v(10.72, 19.45) * mm, "radius": 0.57 * mm});
            skCircle(sketch, "E3.0.15.15", {"center": v(10.72, 21.83) * mm, "radius": 0.57 * mm});
            skCircle(sketch, "E3.0.15.16", {"center": v(10.72, 24.21) * mm, "radius": 0.57 * mm});
            skCircle(sketch, "E3.0.15.17", {"center": v(10.72, 26.6) * mm, "radius": 0.57 * mm});
            skCircle(sketch, "E3.0.16.12", {"center": v(13.1, 14.68) * mm, "radius": 0.57 * mm});
            skCircle(sketch, "E3.0.16.13", {"center": v(13.1, 17.07) * mm, "radius": 0.57 * mm});
            skCircle(sketch, "E3.0.16.14", {"center": v(13.1, 19.45) * mm, "radius": 0.57 * mm});
            skCircle(sketch, "E3.0.16.15", {"center": v(13.1, 21.83) * mm, "radius": 0.57 * mm});
            skCircle(sketch, "E3.0.16.16", {"center": v(13.1, 24.21) * mm, "radius": 0.57 * mm});
            skCircle(sketch, "E3.0.16.17", {"center": v(13.1, 26.6) * mm, "radius": 0.57 * mm});
            skCircle(sketch, "E3.0.17.12", {"center": v(15.49, 14.68) * mm, "radius": 0.57 * mm});
            skCircle(sketch, "E3.0.17.13", {"center": v(15.49, 17.07) * mm, "radius": 0.57 * mm});
            skCircle(sketch, "E3.0.17.14", {"center": v(15.49, 19.45) * mm, "radius": 0.57 * mm});
            skCircle(sketch, "E3.0.17.15", {"center": v(15.49, 21.83) * mm, "radius": 0.57 * mm});
            skCircle(sketch, "E3.0.17.16", {"center": v(15.49, 24.21) * mm, "radius": 0.57 * mm});
            skCircle(sketch, "E3.0.17.17", {"center": v(15.49, 26.6) * mm, "radius": 0.57 * mm});
            skCircle(sketch, "E3.0.18.12", {"center": v(17.87, 14.68) * mm, "radius": 0.57 * mm});
            skCircle(sketch, "E3.0.18.13", {"center": v(17.87, 17.07) * mm, "radius": 0.57 * mm});
            skCircle(sketch, "E3.0.18.14", {"center": v(17.87, 19.45) * mm, "radius": 0.57 * mm});
            skCircle(sketch, "E3.0.18.15", {"center": v(17.87, 21.83) * mm, "radius": 0.57 * mm});
            skCircle(sketch, "E3.0.18.16", {"center": v(17.87, 24.21) * mm, "radius": 0.57 * mm});
            skCircle(sketch, "E3.0.18.17", {"center": v(17.87, 26.6) * mm, "radius": 0.57 * mm});
            skCircle(sketch, "E3.0.19.12", {"center": v(20.25, 14.68) * mm, "radius": 0.57 * mm});
            skCircle(sketch, "E3.0.19.13", {"center": v(20.25, 17.07) * mm, "radius": 0.57 * mm});
            skCircle(sketch, "E3.0.19.14", {"center": v(20.25, 19.45) * mm, "radius": 0.57 * mm});
            skCircle(sketch, "E3.0.19.15", {"center": v(20.25, 21.83) * mm, "radius": 0.57 * mm});
            skCircle(sketch, "E3.0.19.16", {"center": v(20.25, 24.21) * mm, "radius": 0.57 * mm});
            skCircle(sketch, "E3.0.19.17", {"center": v(20.25, 26.6) * mm, "radius": 0.57 * mm});
            skCircle(sketch, "E3.0.20.12", {"center": v(22.63, 14.68) * mm, "radius": 0.57 * mm});
            skCircle(sketch, "E3.0.20.13", {"center": v(22.63, 17.07) * mm, "radius": 0.57 * mm});
            skCircle(sketch, "E3.0.20.14", {"center": v(22.63, 19.45) * mm, "radius": 0.57 * mm});
            skCircle(sketch, "E3.0.20.15", {"center": v(22.63, 21.83) * mm, "radius": 0.57 * mm});
            skCircle(sketch, "E3.0.20.16", {"center": v(22.63, 24.21) * mm, "radius": 0.57 * mm});
            skCircle(sketch, "E3.0.20.17", {"center": v(22.63, 26.6) * mm, "radius": 0.57 * mm});
            skCircle(sketch, "E3.0.21.12", {"center": v(25.02, 14.68) * mm, "radius": 0.57 * mm});
            skCircle(sketch, "E3.0.21.13", {"center": v(25.02, 17.07) * mm, "radius": 0.57 * mm});
            skCircle(sketch, "E3.0.21.14", {"center": v(25.02, 19.45) * mm, "radius": 0.57 * mm});
            skCircle(sketch, "E3.0.21.15", {"center": v(25.02, 21.83) * mm, "radius": 0.57 * mm});
            skCircle(sketch, "E3.0.21.16", {"center": v(25.02, 24.21) * mm, "radius": 0.57 * mm});
            skCircle(sketch, "E3.0.21.17", {"center": v(25.02, 26.6) * mm, "radius": 0.57 * mm});
            skCircle(sketch, "E4.0.0.18", {"center": v(-25.02, 28.98) * mm, "radius": 0.57 * mm});
            skCircle(sketch, "E4.0.1.18", {"center": v(-22.63, 28.98) * mm, "radius": 0.57 * mm});
            skCircle(sketch, "E4.0.2.18", {"center": v(-20.25, 28.98) * mm, "radius": 0.57 * mm});
            skCircle(sketch, "E4.0.3.18", {"center": v(-17.87, 28.98) * mm, "radius": 0.57 * mm});
            skCircle(sketch, "E4.0.4.18", {"center": v(-15.49, 28.98) * mm, "radius": 0.57 * mm});
            skCircle(sketch, "E4.0.5.18", {"center": v(-13.1, 28.98) * mm, "radius": 0.57 * mm});
            skCircle(sketch, "E4.0.6.18", {"center": v(-10.72, 28.98) * mm, "radius": 0.57 * mm});
            skCircle(sketch, "E4.0.7.18", {"center": v(-8.34, 28.98) * mm, "radius": 0.57 * mm});
            skCircle(sketch, "E4.0.8.18", {"center": v(-5.96, 28.98) * mm, "radius": 0.57 * mm});
            skCircle(sketch, "E4.0.9.18", {"center": v(-3.57, 28.98) * mm, "radius": 0.57 * mm});
            skCircle(sketch, "E4.0.10.18", {"center": v(-1.2, 28.98) * mm, "radius": 0.57 * mm});
            skCircle(sketch, "E4.0.11.18", {"center": v(1.2, 28.98) * mm, "radius": 0.57 * mm});
            skCircle(sketch, "E4.0.12.18", {"center": v(3.57, 28.98) * mm, "radius": 0.57 * mm});
            skCircle(sketch, "E4.0.13.18", {"center": v(5.96, 28.98) * mm, "radius": 0.57 * mm});
            skCircle(sketch, "E4.0.14.18", {"center": v(8.34, 28.98) * mm, "radius": 0.57 * mm});
            skCircle(sketch, "E4.0.15.18", {"center": v(10.72, 28.98) * mm, "radius": 0.57 * mm});
            skCircle(sketch, "E4.0.16.18", {"center": v(13.1, 28.98) * mm, "radius": 0.57 * mm});
            skCircle(sketch, "E4.0.17.18", {"center": v(15.49, 28.98) * mm, "radius": 0.57 * mm});
            skCircle(sketch, "E4.0.18.18", {"center": v(17.87, 28.98) * mm, "radius": 0.57 * mm});
            skCircle(sketch, "E4.0.19.18", {"center": v(20.25, 28.98) * mm, "radius": 0.57 * mm});
            skCircle(sketch, "E4.0.20.18", {"center": v(22.63, 28.98) * mm, "radius": 0.57 * mm});
            skCircle(sketch, "E4.0.21.18", {"center": v(25.02, 28.98) * mm, "radius": 0.57 * mm});
            skCircle(sketch, "E5.0.0.19", {"center": v(-25.02, 31.36) * mm, "radius": 0.57 * mm});
            skCircle(sketch, "E5.0.1.19", {"center": v(-22.63, 31.36) * mm, "radius": 0.57 * mm});
            skCircle(sketch, "E5.0.2.19", {"center": v(-20.25, 31.36) * mm, "radius": 0.57 * mm});
            skCircle(sketch, "E5.0.3.19", {"center": v(-17.87, 31.36) * mm, "radius": 0.57 * mm});
            skCircle(sketch, "E5.0.4.19", {"center": v(-15.49, 31.36) * mm, "radius": 0.57 * mm});
            skCircle(sketch, "E5.0.5.19", {"center": v(-13.1, 31.36) * mm, "radius": 0.57 * mm});
            skCircle(sketch, "E5.0.6.19", {"center": v(-10.72, 31.36) * mm, "radius": 0.57 * mm});
            skCircle(sketch, "E5.0.7.19", {"center": v(-8.34, 31.36) * mm, "radius": 0.57 * mm});
            skCircle(sketch, "E5.0.8.19", {"center": v(-5.96, 31.36) * mm, "radius": 0.57 * mm});
            skCircle(sketch, "E5.0.9.19", {"center": v(-3.57, 31.36) * mm, "radius": 0.57 * mm});
            skCircle(sketch, "E5.0.10.19", {"center": v(-1.2, 31.36) * mm, "radius": 0.57 * mm});
            skCircle(sketch, "E5.0.11.19", {"center": v(1.2, 31.36) * mm, "radius": 0.57 * mm});
            skCircle(sketch, "E5.0.12.19", {"center": v(3.57, 31.36) * mm, "radius": 0.57 * mm});
            skCircle(sketch, "E5.0.13.19", {"center": v(5.96, 31.36) * mm, "radius": 0.57 * mm});
            skCircle(sketch, "E5.0.14.19", {"center": v(8.34, 31.36) * mm, "radius": 0.57 * mm});
            skCircle(sketch, "E5.0.15.19", {"center": v(10.72, 31.36) * mm, "radius": 0.57 * mm});
            skCircle(sketch, "E5.0.16.19", {"center": v(13.1, 31.36) * mm, "radius": 0.57 * mm});
            skCircle(sketch, "E5.0.17.19", {"center": v(15.49, 31.36) * mm, "radius": 0.57 * mm});
            skCircle(sketch, "E5.0.18.19", {"center": v(17.87, 31.36) * mm, "radius": 0.57 * mm});
            skCircle(sketch, "E5.0.19.19", {"center": v(20.25, 31.36) * mm, "radius": 0.57 * mm});
            skCircle(sketch, "E5.0.20.19", {"center": v(22.63, 31.36) * mm, "radius": 0.57 * mm});
            skCircle(sketch, "E5.0.21.19", {"center": v(25.02, 31.36) * mm, "radius": 0.57 * mm});
            skSolve(sketch);
        }
        {
            var Q0;
            Q0=qSketchRegion(id+"F2",true);
            extrude(context, id + "F3", {"entities" : qUnion([Q0]), "operationType" : NewBodyOperationType.REMOVE, "oppositeDirection" : true, "depth" : 0.76 * mm, "offsetDistance" : 25.4 * mm});
        }
        {
            var Q0;
            Q0=makeQuery(id+"F1.opExtrude","SWEPT_EDGE",EDGE,{"disambiguationData":[OSD([sQuery(id+"F0.wireOp",EDGE,"E0.top"),sQuery(id+"F0.wireOp",EDGE,"E0.left")])]});
            var Q1;
            Q1=makeQuery(id+"F1.opExtrude","SWEPT_EDGE",EDGE,{"disambiguationData":[OSD([sQuery(id+"F0.wireOp",EDGE,"E0.bottom"),sQuery(id+"F0.wireOp",EDGE,"E0.left")])]});
            var Q2;
            Q2=makeQuery(id+"F1.opExtrude","SWEPT_EDGE",EDGE,{"disambiguationData":[OSD([sQuery(id+"F0.wireOp",EDGE,"E0.bottom"),sQuery(id+"F0.wireOp",EDGE,"E0.right")])]});
            var Q3;
            Q3=makeQuery(id+"F1.opExtrude","SWEPT_EDGE",EDGE,{"disambiguationData":[OSD([sQuery(id+"F0.wireOp",EDGE,"E0.top"),sQuery(id+"F0.wireOp",EDGE,"E0.right")])]});
            fillet(context, id + "F4", {"entities" : qUnion([Q0, Q1, Q2, Q3]), "radius" : 0.76 * mm, "tangentPropagation" : true, "allowEdgeOverflow" : false});
        }
        {
            var Q0;
            Q0=makeQuery(id+"F1.opExtrude","CAP_EDGE",EDGE,{"disambiguationData":[OSD([sQuery(id+"F0.wireOp",EDGE,"E0.right")])],"isStart":false});
            fillet(context, id + "F5", {"entities" : qUnion([Q0]), "radius" : 0.5 * mm, "tangentPropagation" : true, "allowEdgeOverflow" : false});
        }
        {
            var Q0;
            Q0=makeQuery(id+"F1.opExtrude","CAP_EDGE",EDGE,{"disambiguationData":[OSD([sQuery(id+"F0.wireOp",EDGE,"E0.right")])],"isStart":true});
            chamfer(context, id + "F6", {"entities" : qUnion([Q0]), "width" : 0.5 * mm, "tangentPropagation" : true});
        }
        {
            var Q0;
            Q0=makeQuery(id+"F1.opExtrude","CAP_FACE",FACE,{"disambiguationData":[OSD([sQuery(id+"F0.wireOp",EDGE,"E0.bottom"),sQuery(id+"F0.wireOp",EDGE,"E0.top"),sQuery(id+"F0.wireOp",EDGE,"E0.left"),sQuery(id+"F0.wireOp",EDGE,"E0.right")])],"isStart":false});
            var sketch = newSketch(context, id + "F7", { "sketchPlane" : qUnion([Q0])});
            skLineSegment(sketch, "E6.bottom", {"start": v(-19.3, 13.08) * mm, "end": v(19.3, 13.08) * mm});
            skLineSegment(sketch, "E6.top", {"start": v(-19.3, -12.83) * mm, "end": v(19.3, -12.83) * mm});
            skLineSegment(sketch, "E6.left", {"start": v(-19.3, 13.08) * mm, "end": v(-19.3, -12.83) * mm});
            skLineSegment(sketch, "E6.right", {"start": v(19.3, 13.08) * mm, "end": v(19.3, -12.83) * mm});
            skSolve(sketch);
        }
        {
            var Q0;
            Q0=qSketchRegion(id+"F7",true);
            extrude(context, id + "F8", {"entities" : qUnion([Q0]), "operationType" : NewBodyOperationType.REMOVE, "oppositeDirection" : true, "depth" : 0.76 * mm, "offsetDistance" : 25.4 * mm});
        }
        {
            var Q0;
            Q0=makeQuery(id+"F8.boolean.opBoolean","MERGE",FACE,{"derivedFrom":[makeQuery(id+"F3.boolean.opBoolean","COPY",FACE,{"derivedFrom":makeQuery(id+"F3.opExtrude","CAP_FACE",FACE,{"disambiguationData":[OSD([sQuery(id+"F2.wireOp",EDGE,"E2.3.0.0")])],"isStart":false})}),makeQuery(id+"F3.boolean.opBoolean","COPY",FACE,{"derivedFrom":makeQuery(id+"F3.opExtrude","CAP_FACE",FACE,{"disambiguationData":[OSD([sQuery(id+"F2.wireOp",EDGE,"E2.3.1.0")])],"isStart":false})}),makeQuery(id+"F3.boolean.opBoolean","COPY",FACE,{"derivedFrom":makeQuery(id+"F3.opExtrude","CAP_FACE",FACE,{"disambiguationData":[OSD([sQuery(id+"F2.wireOp",EDGE,"E2.3.2.0")])],"isStart":false})}),makeQuery(id+"F3.boolean.opBoolean","COPY",FACE,{"derivedFrom":makeQuery(id+"F3.opExtrude","CAP_FACE",FACE,{"disambiguationData":[OSD([sQuery(id+"F2.wireOp",EDGE,"E2.3.3.0")])],"isStart":false})}),makeQuery(id+"F3.boolean.opBoolean","COPY",FACE,{"derivedFrom":makeQuery(id+"F3.opExtrude","CAP_FACE",FACE,{"disambiguationData":[OSD([sQuery(id+"F2.wireOp",EDGE,"E2.3.4.0")])],"isStart":false})}),makeQuery(id+"F3.boolean.opBoolean","COPY",FACE,{"derivedFrom":makeQuery(id+"F3.opExtrude","CAP_FACE",FACE,{"disambiguationData":[OSD([sQuery(id+"F2.wireOp",EDGE,"E2.3.5.0")])],"isStart":false})}),makeQuery(id+"F3.boolean.opBoolean","COPY",FACE,{"derivedFrom":makeQuery(id+"F3.opExtrude","CAP_FACE",FACE,{"disambiguationData":[OSD([sQuery(id+"F2.wireOp",EDGE,"E2.3.6.0")])],"isStart":false})}),makeQuery(id+"F3.boolean.opBoolean","COPY",FACE,{"derivedFrom":makeQuery(id+"F3.opExtrude","CAP_FACE",FACE,{"disambiguationData":[OSD([sQuery(id+"F2.wireOp",EDGE,"E2.3.7.0")])],"isStart":false})}),makeQuery(id+"F3.boolean.opBoolean","COPY",FACE,{"derivedFrom":makeQuery(id+"F3.opExtrude","CAP_FACE",FACE,{"disambiguationData":[OSD([sQuery(id+"F2.wireOp",EDGE,"E2.3.8.0")])],"isStart":false})}),makeQuery(id+"F3.boolean.opBoolean","COPY",FACE,{"derivedFrom":makeQuery(id+"F3.opExtrude","CAP_FACE",FACE,{"disambiguationData":[OSD([sQuery(id+"F2.wireOp",EDGE,"E2.3.9.0")])],"isStart":false})}),makeQuery(id+"F3.boolean.opBoolean","COPY",FACE,{"derivedFrom":makeQuery(id+"F3.opExtrude","CAP_FACE",FACE,{"disambiguationData":[OSD([sQuery(id+"F2.wireOp",EDGE,"E2.3.10.0")])],"isStart":false})}),makeQuery(id+"F3.boolean.opBoolean","COPY",FACE,{"derivedFrom":makeQuery(id+"F3.opExtrude","CAP_FACE",FACE,{"disambiguationData":[OSD([sQuery(id+"F2.wireOp",EDGE,"E2.3.11.0")])],"isStart":false})}),makeQuery(id+"F3.boolean.opBoolean","COPY",FACE,{"derivedFrom":makeQuery(id+"F3.opExtrude","CAP_FACE",FACE,{"disambiguationData":[OSD([sQuery(id+"F2.wireOp",EDGE,"E2.4.0.0")])],"isStart":false})}),makeQuery(id+"F3.boolean.opBoolean","COPY",FACE,{"derivedFrom":makeQuery(id+"F3.opExtrude","CAP_FACE",FACE,{"disambiguationData":[OSD([sQuery(id+"F2.wireOp",EDGE,"E2.4.1.0")])],"isStart":false})}),makeQuery(id+"F3.boolean.opBoolean","COPY",FACE,{"derivedFrom":makeQuery(id+"F3.opExtrude","CAP_FACE",FACE,{"disambiguationData":[OSD([sQuery(id+"F2.wireOp",EDGE,"E2.4.2.0")])],"isStart":false})}),makeQuery(id+"F3.boolean.opBoolean","COPY",FACE,{"derivedFrom":makeQuery(id+"F3.opExtrude","CAP_FACE",FACE,{"disambiguationData":[OSD([sQuery(id+"F2.wireOp",EDGE,"E2.4.3.0")])],"isStart":false})}),makeQuery(id+"F3.boolean.opBoolean","COPY",FACE,{"derivedFrom":makeQuery(id+"F3.opExtrude","CAP_FACE",FACE,{"disambiguationData":[OSD([sQuery(id+"F2.wireOp",EDGE,"E2.4.4.0")])],"isStart":false})}),makeQuery(id+"F3.boolean.opBoolean","COPY",FACE,{"derivedFrom":makeQuery(id+"F3.opExtrude","CAP_FACE",FACE,{"disambiguationData":[OSD([sQuery(id+"F2.wireOp",EDGE,"E2.4.5.0")])],"isStart":false})}),makeQuery(id+"F3.boolean.opBoolean","COPY",FACE,{"derivedFrom":makeQuery(id+"F3.opExtrude","CAP_FACE",FACE,{"disambiguationData":[OSD([sQuery(id+"F2.wireOp",EDGE,"E2.4.6.0")])],"isStart":false})}),makeQuery(id+"F3.boolean.opBoolean","COPY",FACE,{"derivedFrom":makeQuery(id+"F3.opExtrude","CAP_FACE",FACE,{"disambiguationData":[OSD([sQuery(id+"F2.wireOp",EDGE,"E2.4.7.0")])],"isStart":false})}),makeQuery(id+"F3.boolean.opBoolean","COPY",FACE,{"derivedFrom":makeQuery(id+"F3.opExtrude","CAP_FACE",FACE,{"disambiguationData":[OSD([sQuery(id+"F2.wireOp",EDGE,"E2.4.8.0")])],"isStart":false})}),makeQuery(id+"F3.boolean.opBoolean","COPY",FACE,{"derivedFrom":makeQuery(id+"F3.opExtrude","CAP_FACE",FACE,{"disambiguationData":[OSD([sQuery(id+"F2.wireOp",EDGE,"E2.4.9.0")])],"isStart":false})}),makeQuery(id+"F3.boolean.opBoolean","COPY",FACE,{"derivedFrom":makeQuery(id+"F3.opExtrude","CAP_FACE",FACE,{"disambiguationData":[OSD([sQuery(id+"F2.wireOp",EDGE,"E2.4.10.0")])],"isStart":false})}),makeQuery(id+"F3.boolean.opBoolean","COPY",FACE,{"derivedFrom":makeQuery(id+"F3.opExtrude","CAP_FACE",FACE,{"disambiguationData":[OSD([sQuery(id+"F2.wireOp",EDGE,"E2.4.11.0")])],"isStart":false})}),makeQuery(id+"F3.boolean.opBoolean","COPY",FACE,{"derivedFrom":makeQuery(id+"F3.opExtrude","CAP_FACE",FACE,{"disambiguationData":[OSD([sQuery(id+"F2.wireOp",EDGE,"E2.5.0.0")])],"isStart":false})}),makeQuery(id+"F3.boolean.opBoolean","COPY",FACE,{"derivedFrom":makeQuery(id+"F3.opExtrude","CAP_FACE",FACE,{"disambiguationData":[OSD([sQuery(id+"F2.wireOp",EDGE,"E2.5.1.0")])],"isStart":false})}),makeQuery(id+"F3.boolean.opBoolean","COPY",FACE,{"derivedFrom":makeQuery(id+"F3.opExtrude","CAP_FACE",FACE,{"disambiguationData":[OSD([sQuery(id+"F2.wireOp",EDGE,"E2.5.2.0")])],"isStart":false})}),makeQuery(id+"F3.boolean.opBoolean","COPY",FACE,{"derivedFrom":makeQuery(id+"F3.opExtrude","CAP_FACE",FACE,{"disambiguationData":[OSD([sQuery(id+"F2.wireOp",EDGE,"E2.5.3.0")])],"isStart":false})}),makeQuery(id+"F3.boolean.opBoolean","COPY",FACE,{"derivedFrom":makeQuery(id+"F3.opExtrude","CAP_FACE",FACE,{"disambiguationData":[OSD([sQuery(id+"F2.wireOp",EDGE,"E2.5.4.0")])],"isStart":false})}),makeQuery(id+"F3.boolean.opBoolean","COPY",FACE,{"derivedFrom":makeQuery(id+"F3.opExtrude","CAP_FACE",FACE,{"disambiguationData":[OSD([sQuery(id+"F2.wireOp",EDGE,"E2.5.5.0")])],"isStart":false})}),makeQuery(id+"F3.boolean.opBoolean","COPY",FACE,{"derivedFrom":makeQuery(id+"F3.opExtrude","CAP_FACE",FACE,{"disambiguationData":[OSD([sQuery(id+"F2.wireOp",EDGE,"E2.5.6.0")])],"isStart":false})}),makeQuery(id+"F3.boolean.opBoolean","COPY",FACE,{"derivedFrom":makeQuery(id+"F3.opExtrude","CAP_FACE",FACE,{"disambiguationData":[OSD([sQuery(id+"F2.wireOp",EDGE,"E2.5.7.0")])],"isStart":false})}),makeQuery(id+"F3.boolean.opBoolean","COPY",FACE,{"derivedFrom":makeQuery(id+"F3.opExtrude","CAP_FACE",FACE,{"disambiguationData":[OSD([sQuery(id+"F2.wireOp",EDGE,"E2.5.8.0")])],"isStart":false})}),makeQuery(id+"F3.boolean.opBoolean","COPY",FACE,{"derivedFrom":makeQuery(id+"F3.opExtrude","CAP_FACE",FACE,{"disambiguationData":[OSD([sQuery(id+"F2.wireOp",EDGE,"E2.5.9.0")])],"isStart":false})}),makeQuery(id+"F3.boolean.opBoolean","COPY",FACE,{"derivedFrom":makeQuery(id+"F3.opExtrude","CAP_FACE",FACE,{"disambiguationData":[OSD([sQuery(id+"F2.wireOp",EDGE,"E2.5.10.0")])],"isStart":false})}),makeQuery(id+"F3.boolean.opBoolean","COPY",FACE,{"derivedFrom":makeQuery(id+"F3.opExtrude","CAP_FACE",FACE,{"disambiguationData":[OSD([sQuery(id+"F2.wireOp",EDGE,"E2.5.11.0")])],"isStart":false})}),makeQuery(id+"F3.boolean.opBoolean","COPY",FACE,{"derivedFrom":makeQuery(id+"F3.opExtrude","CAP_FACE",FACE,{"disambiguationData":[OSD([sQuery(id+"F2.wireOp",EDGE,"E2.6.0.0")])],"isStart":false})}),makeQuery(id+"F3.boolean.opBoolean","COPY",FACE,{"derivedFrom":makeQuery(id+"F3.opExtrude","CAP_FACE",FACE,{"disambiguationData":[OSD([sQuery(id+"F2.wireOp",EDGE,"E2.6.1.0")])],"isStart":false})}),makeQuery(id+"F3.boolean.opBoolean","COPY",FACE,{"derivedFrom":makeQuery(id+"F3.opExtrude","CAP_FACE",FACE,{"disambiguationData":[OSD([sQuery(id+"F2.wireOp",EDGE,"E2.6.2.0")])],"isStart":false})}),makeQuery(id+"F3.boolean.opBoolean","COPY",FACE,{"derivedFrom":makeQuery(id+"F3.opExtrude","CAP_FACE",FACE,{"disambiguationData":[OSD([sQuery(id+"F2.wireOp",EDGE,"E2.6.3.0")])],"isStart":false})}),makeQuery(id+"F3.boolean.opBoolean","COPY",FACE,{"derivedFrom":makeQuery(id+"F3.opExtrude","CAP_FACE",FACE,{"disambiguationData":[OSD([sQuery(id+"F2.wireOp",EDGE,"E2.6.4.0")])],"isStart":false})}),makeQuery(id+"F3.boolean.opBoolean","COPY",FACE,{"derivedFrom":makeQuery(id+"F3.opExtrude","CAP_FACE",FACE,{"disambiguationData":[OSD([sQuery(id+"F2.wireOp",EDGE,"E2.6.5.0")])],"isStart":false})}),makeQuery(id+"F3.boolean.opBoolean","COPY",FACE,{"derivedFrom":makeQuery(id+"F3.opExtrude","CAP_FACE",FACE,{"disambiguationData":[OSD([sQuery(id+"F2.wireOp",EDGE,"E2.6.6.0")])],"isStart":false})}),makeQuery(id+"F3.boolean.opBoolean","COPY",FACE,{"derivedFrom":makeQuery(id+"F3.opExtrude","CAP_FACE",FACE,{"disambiguationData":[OSD([sQuery(id+"F2.wireOp",EDGE,"E2.6.7.0")])],"isStart":false})}),makeQuery(id+"F3.boolean.opBoolean","COPY",FACE,{"derivedFrom":makeQuery(id+"F3.opExtrude","CAP_FACE",FACE,{"disambiguationData":[OSD([sQuery(id+"F2.wireOp",EDGE,"E2.6.8.0")])],"isStart":false})}),makeQuery(id+"F3.boolean.opBoolean","COPY",FACE,{"derivedFrom":makeQuery(id+"F3.opExtrude","CAP_FACE",FACE,{"disambiguationData":[OSD([sQuery(id+"F2.wireOp",EDGE,"E2.6.9.0")])],"isStart":false})}),makeQuery(id+"F3.boolean.opBoolean","COPY",FACE,{"derivedFrom":makeQuery(id+"F3.opExtrude","CAP_FACE",FACE,{"disambiguationData":[OSD([sQuery(id+"F2.wireOp",EDGE,"E2.6.10.0")])],"isStart":false})}),makeQuery(id+"F3.boolean.opBoolean","COPY",FACE,{"derivedFrom":makeQuery(id+"F3.opExtrude","CAP_FACE",FACE,{"disambiguationData":[OSD([sQuery(id+"F2.wireOp",EDGE,"E2.6.11.0")])],"isStart":false})}),makeQuery(id+"F3.boolean.opBoolean","COPY",FACE,{"derivedFrom":makeQuery(id+"F3.opExtrude","CAP_FACE",FACE,{"disambiguationData":[OSD([sQuery(id+"F2.wireOp",EDGE,"E2.7.0.0")])],"isStart":false})}),makeQuery(id+"F3.boolean.opBoolean","COPY",FACE,{"derivedFrom":makeQuery(id+"F3.opExtrude","CAP_FACE",FACE,{"disambiguationData":[OSD([sQuery(id+"F2.wireOp",EDGE,"E2.7.1.0")])],"isStart":false})}),makeQuery(id+"F3.boolean.opBoolean","COPY",FACE,{"derivedFrom":makeQuery(id+"F3.opExtrude","CAP_FACE",FACE,{"disambiguationData":[OSD([sQuery(id+"F2.wireOp",EDGE,"E2.7.2.0")])],"isStart":false})}),makeQuery(id+"F3.boolean.opBoolean","COPY",FACE,{"derivedFrom":makeQuery(id+"F3.opExtrude","CAP_FACE",FACE,{"disambiguationData":[OSD([sQuery(id+"F2.wireOp",EDGE,"E2.7.3.0")])],"isStart":false})}),makeQuery(id+"F3.boolean.opBoolean","COPY",FACE,{"derivedFrom":makeQuery(id+"F3.opExtrude","CAP_FACE",FACE,{"disambiguationData":[OSD([sQuery(id+"F2.wireOp",EDGE,"E2.7.4.0")])],"isStart":false})}),makeQuery(id+"F3.boolean.opBoolean","COPY",FACE,{"derivedFrom":makeQuery(id+"F3.opExtrude","CAP_FACE",FACE,{"disambiguationData":[OSD([sQuery(id+"F2.wireOp",EDGE,"E2.7.5.0")])],"isStart":false})}),makeQuery(id+"F3.boolean.opBoolean","COPY",FACE,{"derivedFrom":makeQuery(id+"F3.opExtrude","CAP_FACE",FACE,{"disambiguationData":[OSD([sQuery(id+"F2.wireOp",EDGE,"E2.7.6.0")])],"isStart":false})}),makeQuery(id+"F3.boolean.opBoolean","COPY",FACE,{"derivedFrom":makeQuery(id+"F3.opExtrude","CAP_FACE",FACE,{"disambiguationData":[OSD([sQuery(id+"F2.wireOp",EDGE,"E2.7.7.0")])],"isStart":false})}),makeQuery(id+"F3.boolean.opBoolean","COPY",FACE,{"derivedFrom":makeQuery(id+"F3.opExtrude","CAP_FACE",FACE,{"disambiguationData":[OSD([sQuery(id+"F2.wireOp",EDGE,"E2.7.8.0")])],"isStart":false})}),makeQuery(id+"F3.boolean.opBoolean","COPY",FACE,{"derivedFrom":makeQuery(id+"F3.opExtrude","CAP_FACE",FACE,{"disambiguationData":[OSD([sQuery(id+"F2.wireOp",EDGE,"E2.7.9.0")])],"isStart":false})}),makeQuery(id+"F3.boolean.opBoolean","COPY",FACE,{"derivedFrom":makeQuery(id+"F3.opExtrude","CAP_FACE",FACE,{"disambiguationData":[OSD([sQuery(id+"F2.wireOp",EDGE,"E2.7.10.0")])],"isStart":false})}),makeQuery(id+"F3.boolean.opBoolean","COPY",FACE,{"derivedFrom":makeQuery(id+"F3.opExtrude","CAP_FACE",FACE,{"disambiguationData":[OSD([sQuery(id+"F2.wireOp",EDGE,"E2.7.11.0")])],"isStart":false})}),makeQuery(id+"F3.boolean.opBoolean","COPY",FACE,{"derivedFrom":makeQuery(id+"F3.opExtrude","CAP_FACE",FACE,{"disambiguationData":[OSD([sQuery(id+"F2.wireOp",EDGE,"E2.8.0.0")])],"isStart":false})}),makeQuery(id+"F3.boolean.opBoolean","COPY",FACE,{"derivedFrom":makeQuery(id+"F3.opExtrude","CAP_FACE",FACE,{"disambiguationData":[OSD([sQuery(id+"F2.wireOp",EDGE,"E2.8.1.0")])],"isStart":false})}),makeQuery(id+"F3.boolean.opBoolean","COPY",FACE,{"derivedFrom":makeQuery(id+"F3.opExtrude","CAP_FACE",FACE,{"disambiguationData":[OSD([sQuery(id+"F2.wireOp",EDGE,"E2.8.2.0")])],"isStart":false})}),makeQuery(id+"F3.boolean.opBoolean","COPY",FACE,{"derivedFrom":makeQuery(id+"F3.opExtrude","CAP_FACE",FACE,{"disambiguationData":[OSD([sQuery(id+"F2.wireOp",EDGE,"E2.8.3.0")])],"isStart":false})}),makeQuery(id+"F3.boolean.opBoolean","COPY",FACE,{"derivedFrom":makeQuery(id+"F3.opExtrude","CAP_FACE",FACE,{"disambiguationData":[OSD([sQuery(id+"F2.wireOp",EDGE,"E2.8.4.0")])],"isStart":false})}),makeQuery(id+"F3.boolean.opBoolean","COPY",FACE,{"derivedFrom":makeQuery(id+"F3.opExtrude","CAP_FACE",FACE,{"disambiguationData":[OSD([sQuery(id+"F2.wireOp",EDGE,"E2.8.5.0")])],"isStart":false})}),makeQuery(id+"F3.boolean.opBoolean","COPY",FACE,{"derivedFrom":makeQuery(id+"F3.opExtrude","CAP_FACE",FACE,{"disambiguationData":[OSD([sQuery(id+"F2.wireOp",EDGE,"E2.8.6.0")])],"isStart":false})}),makeQuery(id+"F3.boolean.opBoolean","COPY",FACE,{"derivedFrom":makeQuery(id+"F3.opExtrude","CAP_FACE",FACE,{"disambiguationData":[OSD([sQuery(id+"F2.wireOp",EDGE,"E2.8.7.0")])],"isStart":false})}),makeQuery(id+"F3.boolean.opBoolean","COPY",FACE,{"derivedFrom":makeQuery(id+"F3.opExtrude","CAP_FACE",FACE,{"disambiguationData":[OSD([sQuery(id+"F2.wireOp",EDGE,"E2.8.8.0")])],"isStart":false})}),makeQuery(id+"F3.boolean.opBoolean","COPY",FACE,{"derivedFrom":makeQuery(id+"F3.opExtrude","CAP_FACE",FACE,{"disambiguationData":[OSD([sQuery(id+"F2.wireOp",EDGE,"E2.8.9.0")])],"isStart":false})}),makeQuery(id+"F3.boolean.opBoolean","COPY",FACE,{"derivedFrom":makeQuery(id+"F3.opExtrude","CAP_FACE",FACE,{"disambiguationData":[OSD([sQuery(id+"F2.wireOp",EDGE,"E2.8.10.0")])],"isStart":false})}),makeQuery(id+"F3.boolean.opBoolean","COPY",FACE,{"derivedFrom":makeQuery(id+"F3.opExtrude","CAP_FACE",FACE,{"disambiguationData":[OSD([sQuery(id+"F2.wireOp",EDGE,"E2.8.11.0")])],"isStart":false})}),makeQuery(id+"F3.boolean.opBoolean","COPY",FACE,{"derivedFrom":makeQuery(id+"F3.opExtrude","CAP_FACE",FACE,{"disambiguationData":[OSD([sQuery(id+"F2.wireOp",EDGE,"E2.9.0.0")])],"isStart":false})}),makeQuery(id+"F3.boolean.opBoolean","COPY",FACE,{"derivedFrom":makeQuery(id+"F3.opExtrude","CAP_FACE",FACE,{"disambiguationData":[OSD([sQuery(id+"F2.wireOp",EDGE,"E2.9.1.0")])],"isStart":false})}),makeQuery(id+"F3.boolean.opBoolean","COPY",FACE,{"derivedFrom":makeQuery(id+"F3.opExtrude","CAP_FACE",FACE,{"disambiguationData":[OSD([sQuery(id+"F2.wireOp",EDGE,"E2.9.2.0")])],"isStart":false})}),makeQuery(id+"F3.boolean.opBoolean","COPY",FACE,{"derivedFrom":makeQuery(id+"F3.opExtrude","CAP_FACE",FACE,{"disambiguationData":[OSD([sQuery(id+"F2.wireOp",EDGE,"E2.9.3.0")])],"isStart":false})}),makeQuery(id+"F3.boolean.opBoolean","COPY",FACE,{"derivedFrom":makeQuery(id+"F3.opExtrude","CAP_FACE",FACE,{"disambiguationData":[OSD([sQuery(id+"F2.wireOp",EDGE,"E2.9.4.0")])],"isStart":false})}),makeQuery(id+"F3.boolean.opBoolean","COPY",FACE,{"derivedFrom":makeQuery(id+"F3.opExtrude","CAP_FACE",FACE,{"disambiguationData":[OSD([sQuery(id+"F2.wireOp",EDGE,"E2.9.5.0")])],"isStart":false})}),makeQuery(id+"F3.boolean.opBoolean","COPY",FACE,{"derivedFrom":makeQuery(id+"F3.opExtrude","CAP_FACE",FACE,{"disambiguationData":[OSD([sQuery(id+"F2.wireOp",EDGE,"E2.9.6.0")])],"isStart":false})}),makeQuery(id+"F3.boolean.opBoolean","COPY",FACE,{"derivedFrom":makeQuery(id+"F3.opExtrude","CAP_FACE",FACE,{"disambiguationData":[OSD([sQuery(id+"F2.wireOp",EDGE,"E2.9.7.0")])],"isStart":false})}),makeQuery(id+"F3.boolean.opBoolean","COPY",FACE,{"derivedFrom":makeQuery(id+"F3.opExtrude","CAP_FACE",FACE,{"disambiguationData":[OSD([sQuery(id+"F2.wireOp",EDGE,"E2.9.8.0")])],"isStart":false})}),makeQuery(id+"F3.boolean.opBoolean","COPY",FACE,{"derivedFrom":makeQuery(id+"F3.opExtrude","CAP_FACE",FACE,{"disambiguationData":[OSD([sQuery(id+"F2.wireOp",EDGE,"E2.9.9.0")])],"isStart":false})}),makeQuery(id+"F3.boolean.opBoolean","COPY",FACE,{"derivedFrom":makeQuery(id+"F3.opExtrude","CAP_FACE",FACE,{"disambiguationData":[OSD([sQuery(id+"F2.wireOp",EDGE,"E2.9.10.0")])],"isStart":false})}),makeQuery(id+"F3.boolean.opBoolean","COPY",FACE,{"derivedFrom":makeQuery(id+"F3.opExtrude","CAP_FACE",FACE,{"disambiguationData":[OSD([sQuery(id+"F2.wireOp",EDGE,"E2.9.11.0")])],"isStart":false})}),makeQuery(id+"F3.boolean.opBoolean","COPY",FACE,{"derivedFrom":makeQuery(id+"F3.opExtrude","CAP_FACE",FACE,{"disambiguationData":[OSD([sQuery(id+"F2.wireOp",EDGE,"E2.10.0.0")])],"isStart":false})}),makeQuery(id+"F3.boolean.opBoolean","COPY",FACE,{"derivedFrom":makeQuery(id+"F3.opExtrude","CAP_FACE",FACE,{"disambiguationData":[OSD([sQuery(id+"F2.wireOp",EDGE,"E2.10.1.0")])],"isStart":false})}),makeQuery(id+"F3.boolean.opBoolean","COPY",FACE,{"derivedFrom":makeQuery(id+"F3.opExtrude","CAP_FACE",FACE,{"disambiguationData":[OSD([sQuery(id+"F2.wireOp",EDGE,"E2.10.2.0")])],"isStart":false})}),makeQuery(id+"F3.boolean.opBoolean","COPY",FACE,{"derivedFrom":makeQuery(id+"F3.opExtrude","CAP_FACE",FACE,{"disambiguationData":[OSD([sQuery(id+"F2.wireOp",EDGE,"E2.10.3.0")])],"isStart":false})}),makeQuery(id+"F3.boolean.opBoolean","COPY",FACE,{"derivedFrom":makeQuery(id+"F3.opExtrude","CAP_FACE",FACE,{"disambiguationData":[OSD([sQuery(id+"F2.wireOp",EDGE,"E2.10.4.0")])],"isStart":false})}),makeQuery(id+"F3.boolean.opBoolean","COPY",FACE,{"derivedFrom":makeQuery(id+"F3.opExtrude","CAP_FACE",FACE,{"disambiguationData":[OSD([sQuery(id+"F2.wireOp",EDGE,"E2.10.5.0")])],"isStart":false})}),makeQuery(id+"F3.boolean.opBoolean","COPY",FACE,{"derivedFrom":makeQuery(id+"F3.opExtrude","CAP_FACE",FACE,{"disambiguationData":[OSD([sQuery(id+"F2.wireOp",EDGE,"E2.10.6.0")])],"isStart":false})}),makeQuery(id+"F3.boolean.opBoolean","COPY",FACE,{"derivedFrom":makeQuery(id+"F3.opExtrude","CAP_FACE",FACE,{"disambiguationData":[OSD([sQuery(id+"F2.wireOp",EDGE,"E2.10.7.0")])],"isStart":false})}),makeQuery(id+"F3.boolean.opBoolean","COPY",FACE,{"derivedFrom":makeQuery(id+"F3.opExtrude","CAP_FACE",FACE,{"disambiguationData":[OSD([sQuery(id+"F2.wireOp",EDGE,"E2.10.8.0")])],"isStart":false})}),makeQuery(id+"F3.boolean.opBoolean","COPY",FACE,{"derivedFrom":makeQuery(id+"F3.opExtrude","CAP_FACE",FACE,{"disambiguationData":[OSD([sQuery(id+"F2.wireOp",EDGE,"E2.10.9.0")])],"isStart":false})}),makeQuery(id+"F3.boolean.opBoolean","COPY",FACE,{"derivedFrom":makeQuery(id+"F3.opExtrude","CAP_FACE",FACE,{"disambiguationData":[OSD([sQuery(id+"F2.wireOp",EDGE,"E2.10.10.0")])],"isStart":false})}),makeQuery(id+"F3.boolean.opBoolean","COPY",FACE,{"derivedFrom":makeQuery(id+"F3.opExtrude","CAP_FACE",FACE,{"disambiguationData":[OSD([sQuery(id+"F2.wireOp",EDGE,"E2.10.11.0")])],"isStart":false})}),makeQuery(id+"F3.boolean.opBoolean","COPY",FACE,{"derivedFrom":makeQuery(id+"F3.opExtrude","CAP_FACE",FACE,{"disambiguationData":[OSD([sQuery(id+"F2.wireOp",EDGE,"E2.11.0.0")])],"isStart":false})}),makeQuery(id+"F3.boolean.opBoolean","COPY",FACE,{"derivedFrom":makeQuery(id+"F3.opExtrude","CAP_FACE",FACE,{"disambiguationData":[OSD([sQuery(id+"F2.wireOp",EDGE,"E2.11.1.0")])],"isStart":false})}),makeQuery(id+"F3.boolean.opBoolean","COPY",FACE,{"derivedFrom":makeQuery(id+"F3.opExtrude","CAP_FACE",FACE,{"disambiguationData":[OSD([sQuery(id+"F2.wireOp",EDGE,"E2.11.2.0")])],"isStart":false})}),makeQuery(id+"F3.boolean.opBoolean","COPY",FACE,{"derivedFrom":makeQuery(id+"F3.opExtrude","CAP_FACE",FACE,{"disambiguationData":[OSD([sQuery(id+"F2.wireOp",EDGE,"E2.11.3.0")])],"isStart":false})}),makeQuery(id+"F3.boolean.opBoolean","COPY",FACE,{"derivedFrom":makeQuery(id+"F3.opExtrude","CAP_FACE",FACE,{"disambiguationData":[OSD([sQuery(id+"F2.wireOp",EDGE,"E2.11.4.0")])],"isStart":false})}),makeQuery(id+"F3.boolean.opBoolean","COPY",FACE,{"derivedFrom":makeQuery(id+"F3.opExtrude","CAP_FACE",FACE,{"disambiguationData":[OSD([sQuery(id+"F2.wireOp",EDGE,"E2.11.5.0")])],"isStart":false})}),makeQuery(id+"F3.boolean.opBoolean","COPY",FACE,{"derivedFrom":makeQuery(id+"F3.opExtrude","CAP_FACE",FACE,{"disambiguationData":[OSD([sQuery(id+"F2.wireOp",EDGE,"E2.11.6.0")])],"isStart":false})}),makeQuery(id+"F3.boolean.opBoolean","COPY",FACE,{"derivedFrom":makeQuery(id+"F3.opExtrude","CAP_FACE",FACE,{"disambiguationData":[OSD([sQuery(id+"F2.wireOp",EDGE,"E2.11.7.0")])],"isStart":false})}),makeQuery(id+"F3.boolean.opBoolean","COPY",FACE,{"derivedFrom":makeQuery(id+"F3.opExtrude","CAP_FACE",FACE,{"disambiguationData":[OSD([sQuery(id+"F2.wireOp",EDGE,"E2.11.8.0")])],"isStart":false})}),makeQuery(id+"F3.boolean.opBoolean","COPY",FACE,{"derivedFrom":makeQuery(id+"F3.opExtrude","CAP_FACE",FACE,{"disambiguationData":[OSD([sQuery(id+"F2.wireOp",EDGE,"E2.11.9.0")])],"isStart":false})}),makeQuery(id+"F3.boolean.opBoolean","COPY",FACE,{"derivedFrom":makeQuery(id+"F3.opExtrude","CAP_FACE",FACE,{"disambiguationData":[OSD([sQuery(id+"F2.wireOp",EDGE,"E2.11.10.0")])],"isStart":false})}),makeQuery(id+"F3.boolean.opBoolean","COPY",FACE,{"derivedFrom":makeQuery(id+"F3.opExtrude","CAP_FACE",FACE,{"disambiguationData":[OSD([sQuery(id+"F2.wireOp",EDGE,"E2.11.11.0")])],"isStart":false})}),makeQuery(id+"F3.boolean.opBoolean","COPY",FACE,{"derivedFrom":makeQuery(id+"F3.opExtrude","CAP_FACE",FACE,{"disambiguationData":[OSD([sQuery(id+"F2.wireOp",EDGE,"E2.12.0.0")])],"isStart":false})}),makeQuery(id+"F3.boolean.opBoolean","COPY",FACE,{"derivedFrom":makeQuery(id+"F3.opExtrude","CAP_FACE",FACE,{"disambiguationData":[OSD([sQuery(id+"F2.wireOp",EDGE,"E2.12.1.0")])],"isStart":false})}),makeQuery(id+"F3.boolean.opBoolean","COPY",FACE,{"derivedFrom":makeQuery(id+"F3.opExtrude","CAP_FACE",FACE,{"disambiguationData":[OSD([sQuery(id+"F2.wireOp",EDGE,"E2.12.2.0")])],"isStart":false})}),makeQuery(id+"F3.boolean.opBoolean","COPY",FACE,{"derivedFrom":makeQuery(id+"F3.opExtrude","CAP_FACE",FACE,{"disambiguationData":[OSD([sQuery(id+"F2.wireOp",EDGE,"E2.12.3.0")])],"isStart":false})}),makeQuery(id+"F3.boolean.opBoolean","COPY",FACE,{"derivedFrom":makeQuery(id+"F3.opExtrude","CAP_FACE",FACE,{"disambiguationData":[OSD([sQuery(id+"F2.wireOp",EDGE,"E2.12.4.0")])],"isStart":false})}),makeQuery(id+"F3.boolean.opBoolean","COPY",FACE,{"derivedFrom":makeQuery(id+"F3.opExtrude","CAP_FACE",FACE,{"disambiguationData":[OSD([sQuery(id+"F2.wireOp",EDGE,"E2.12.5.0")])],"isStart":false})}),makeQuery(id+"F3.boolean.opBoolean","COPY",FACE,{"derivedFrom":makeQuery(id+"F3.opExtrude","CAP_FACE",FACE,{"disambiguationData":[OSD([sQuery(id+"F2.wireOp",EDGE,"E2.12.6.0")])],"isStart":false})}),makeQuery(id+"F3.boolean.opBoolean","COPY",FACE,{"derivedFrom":makeQuery(id+"F3.opExtrude","CAP_FACE",FACE,{"disambiguationData":[OSD([sQuery(id+"F2.wireOp",EDGE,"E2.12.7.0")])],"isStart":false})}),makeQuery(id+"F3.boolean.opBoolean","COPY",FACE,{"derivedFrom":makeQuery(id+"F3.opExtrude","CAP_FACE",FACE,{"disambiguationData":[OSD([sQuery(id+"F2.wireOp",EDGE,"E2.12.8.0")])],"isStart":false})}),makeQuery(id+"F3.boolean.opBoolean","COPY",FACE,{"derivedFrom":makeQuery(id+"F3.opExtrude","CAP_FACE",FACE,{"disambiguationData":[OSD([sQuery(id+"F2.wireOp",EDGE,"E2.12.9.0")])],"isStart":false})}),makeQuery(id+"F3.boolean.opBoolean","COPY",FACE,{"derivedFrom":makeQuery(id+"F3.opExtrude","CAP_FACE",FACE,{"disambiguationData":[OSD([sQuery(id+"F2.wireOp",EDGE,"E2.12.10.0")])],"isStart":false})}),makeQuery(id+"F3.boolean.opBoolean","COPY",FACE,{"derivedFrom":makeQuery(id+"F3.opExtrude","CAP_FACE",FACE,{"disambiguationData":[OSD([sQuery(id+"F2.wireOp",EDGE,"E2.12.11.0")])],"isStart":false})}),makeQuery(id+"F3.boolean.opBoolean","COPY",FACE,{"derivedFrom":makeQuery(id+"F3.opExtrude","CAP_FACE",FACE,{"disambiguationData":[OSD([sQuery(id+"F2.wireOp",EDGE,"E2.13.0.0")])],"isStart":false})}),makeQuery(id+"F3.boolean.opBoolean","COPY",FACE,{"derivedFrom":makeQuery(id+"F3.opExtrude","CAP_FACE",FACE,{"disambiguationData":[OSD([sQuery(id+"F2.wireOp",EDGE,"E2.13.1.0")])],"isStart":false})}),makeQuery(id+"F3.boolean.opBoolean","COPY",FACE,{"derivedFrom":makeQuery(id+"F3.opExtrude","CAP_FACE",FACE,{"disambiguationData":[OSD([sQuery(id+"F2.wireOp",EDGE,"E2.13.2.0")])],"isStart":false})}),makeQuery(id+"F3.boolean.opBoolean","COPY",FACE,{"derivedFrom":makeQuery(id+"F3.opExtrude","CAP_FACE",FACE,{"disambiguationData":[OSD([sQuery(id+"F2.wireOp",EDGE,"E2.13.3.0")])],"isStart":false})}),makeQuery(id+"F3.boolean.opBoolean","COPY",FACE,{"derivedFrom":makeQuery(id+"F3.opExtrude","CAP_FACE",FACE,{"disambiguationData":[OSD([sQuery(id+"F2.wireOp",EDGE,"E2.13.4.0")])],"isStart":false})}),makeQuery(id+"F3.boolean.opBoolean","COPY",FACE,{"derivedFrom":makeQuery(id+"F3.opExtrude","CAP_FACE",FACE,{"disambiguationData":[OSD([sQuery(id+"F2.wireOp",EDGE,"E2.13.5.0")])],"isStart":false})}),makeQuery(id+"F3.boolean.opBoolean","COPY",FACE,{"derivedFrom":makeQuery(id+"F3.opExtrude","CAP_FACE",FACE,{"disambiguationData":[OSD([sQuery(id+"F2.wireOp",EDGE,"E2.13.6.0")])],"isStart":false})}),makeQuery(id+"F3.boolean.opBoolean","COPY",FACE,{"derivedFrom":makeQuery(id+"F3.opExtrude","CAP_FACE",FACE,{"disambiguationData":[OSD([sQuery(id+"F2.wireOp",EDGE,"E2.13.7.0")])],"isStart":false})}),makeQuery(id+"F3.boolean.opBoolean","COPY",FACE,{"derivedFrom":makeQuery(id+"F3.opExtrude","CAP_FACE",FACE,{"disambiguationData":[OSD([sQuery(id+"F2.wireOp",EDGE,"E2.13.8.0")])],"isStart":false})}),makeQuery(id+"F3.boolean.opBoolean","COPY",FACE,{"derivedFrom":makeQuery(id+"F3.opExtrude","CAP_FACE",FACE,{"disambiguationData":[OSD([sQuery(id+"F2.wireOp",EDGE,"E2.13.9.0")])],"isStart":false})}),makeQuery(id+"F3.boolean.opBoolean","COPY",FACE,{"derivedFrom":makeQuery(id+"F3.opExtrude","CAP_FACE",FACE,{"disambiguationData":[OSD([sQuery(id+"F2.wireOp",EDGE,"E2.13.10.0")])],"isStart":false})}),makeQuery(id+"F3.boolean.opBoolean","COPY",FACE,{"derivedFrom":makeQuery(id+"F3.opExtrude","CAP_FACE",FACE,{"disambiguationData":[OSD([sQuery(id+"F2.wireOp",EDGE,"E2.13.11.0")])],"isStart":false})}),makeQuery(id+"F3.boolean.opBoolean","COPY",FACE,{"derivedFrom":makeQuery(id+"F3.opExtrude","CAP_FACE",FACE,{"disambiguationData":[OSD([sQuery(id+"F2.wireOp",EDGE,"E2.14.0.0")])],"isStart":false})}),makeQuery(id+"F3.boolean.opBoolean","COPY",FACE,{"derivedFrom":makeQuery(id+"F3.opExtrude","CAP_FACE",FACE,{"disambiguationData":[OSD([sQuery(id+"F2.wireOp",EDGE,"E2.14.1.0")])],"isStart":false})}),makeQuery(id+"F3.boolean.opBoolean","COPY",FACE,{"derivedFrom":makeQuery(id+"F3.opExtrude","CAP_FACE",FACE,{"disambiguationData":[OSD([sQuery(id+"F2.wireOp",EDGE,"E2.14.2.0")])],"isStart":false})}),makeQuery(id+"F3.boolean.opBoolean","COPY",FACE,{"derivedFrom":makeQuery(id+"F3.opExtrude","CAP_FACE",FACE,{"disambiguationData":[OSD([sQuery(id+"F2.wireOp",EDGE,"E2.14.3.0")])],"isStart":false})}),makeQuery(id+"F3.boolean.opBoolean","COPY",FACE,{"derivedFrom":makeQuery(id+"F3.opExtrude","CAP_FACE",FACE,{"disambiguationData":[OSD([sQuery(id+"F2.wireOp",EDGE,"E2.14.4.0")])],"isStart":false})}),makeQuery(id+"F3.boolean.opBoolean","COPY",FACE,{"derivedFrom":makeQuery(id+"F3.opExtrude","CAP_FACE",FACE,{"disambiguationData":[OSD([sQuery(id+"F2.wireOp",EDGE,"E2.14.5.0")])],"isStart":false})}),makeQuery(id+"F3.boolean.opBoolean","COPY",FACE,{"derivedFrom":makeQuery(id+"F3.opExtrude","CAP_FACE",FACE,{"disambiguationData":[OSD([sQuery(id+"F2.wireOp",EDGE,"E2.14.6.0")])],"isStart":false})}),makeQuery(id+"F3.boolean.opBoolean","COPY",FACE,{"derivedFrom":makeQuery(id+"F3.opExtrude","CAP_FACE",FACE,{"disambiguationData":[OSD([sQuery(id+"F2.wireOp",EDGE,"E2.14.7.0")])],"isStart":false})}),makeQuery(id+"F3.boolean.opBoolean","COPY",FACE,{"derivedFrom":makeQuery(id+"F3.opExtrude","CAP_FACE",FACE,{"disambiguationData":[OSD([sQuery(id+"F2.wireOp",EDGE,"E2.14.8.0")])],"isStart":false})}),makeQuery(id+"F3.boolean.opBoolean","COPY",FACE,{"derivedFrom":makeQuery(id+"F3.opExtrude","CAP_FACE",FACE,{"disambiguationData":[OSD([sQuery(id+"F2.wireOp",EDGE,"E2.14.9.0")])],"isStart":false})}),makeQuery(id+"F3.boolean.opBoolean","COPY",FACE,{"derivedFrom":makeQuery(id+"F3.opExtrude","CAP_FACE",FACE,{"disambiguationData":[OSD([sQuery(id+"F2.wireOp",EDGE,"E2.14.10.0")])],"isStart":false})}),makeQuery(id+"F3.boolean.opBoolean","COPY",FACE,{"derivedFrom":makeQuery(id+"F3.opExtrude","CAP_FACE",FACE,{"disambiguationData":[OSD([sQuery(id+"F2.wireOp",EDGE,"E2.14.11.0")])],"isStart":false})}),makeQuery(id+"F3.boolean.opBoolean","COPY",FACE,{"derivedFrom":makeQuery(id+"F3.opExtrude","CAP_FACE",FACE,{"disambiguationData":[OSD([sQuery(id+"F2.wireOp",EDGE,"E2.15.0.0")])],"isStart":false})}),makeQuery(id+"F3.boolean.opBoolean","COPY",FACE,{"derivedFrom":makeQuery(id+"F3.opExtrude","CAP_FACE",FACE,{"disambiguationData":[OSD([sQuery(id+"F2.wireOp",EDGE,"E2.15.1.0")])],"isStart":false})}),makeQuery(id+"F3.boolean.opBoolean","COPY",FACE,{"derivedFrom":makeQuery(id+"F3.opExtrude","CAP_FACE",FACE,{"disambiguationData":[OSD([sQuery(id+"F2.wireOp",EDGE,"E2.15.2.0")])],"isStart":false})}),makeQuery(id+"F3.boolean.opBoolean","COPY",FACE,{"derivedFrom":makeQuery(id+"F3.opExtrude","CAP_FACE",FACE,{"disambiguationData":[OSD([sQuery(id+"F2.wireOp",EDGE,"E2.15.3.0")])],"isStart":false})}),makeQuery(id+"F3.boolean.opBoolean","COPY",FACE,{"derivedFrom":makeQuery(id+"F3.opExtrude","CAP_FACE",FACE,{"disambiguationData":[OSD([sQuery(id+"F2.wireOp",EDGE,"E2.15.4.0")])],"isStart":false})}),makeQuery(id+"F3.boolean.opBoolean","COPY",FACE,{"derivedFrom":makeQuery(id+"F3.opExtrude","CAP_FACE",FACE,{"disambiguationData":[OSD([sQuery(id+"F2.wireOp",EDGE,"E2.15.5.0")])],"isStart":false})}),makeQuery(id+"F3.boolean.opBoolean","COPY",FACE,{"derivedFrom":makeQuery(id+"F3.opExtrude","CAP_FACE",FACE,{"disambiguationData":[OSD([sQuery(id+"F2.wireOp",EDGE,"E2.15.6.0")])],"isStart":false})}),makeQuery(id+"F3.boolean.opBoolean","COPY",FACE,{"derivedFrom":makeQuery(id+"F3.opExtrude","CAP_FACE",FACE,{"disambiguationData":[OSD([sQuery(id+"F2.wireOp",EDGE,"E2.15.7.0")])],"isStart":false})}),makeQuery(id+"F3.boolean.opBoolean","COPY",FACE,{"derivedFrom":makeQuery(id+"F3.opExtrude","CAP_FACE",FACE,{"disambiguationData":[OSD([sQuery(id+"F2.wireOp",EDGE,"E2.15.8.0")])],"isStart":false})}),makeQuery(id+"F3.boolean.opBoolean","COPY",FACE,{"derivedFrom":makeQuery(id+"F3.opExtrude","CAP_FACE",FACE,{"disambiguationData":[OSD([sQuery(id+"F2.wireOp",EDGE,"E2.15.9.0")])],"isStart":false})}),makeQuery(id+"F3.boolean.opBoolean","COPY",FACE,{"derivedFrom":makeQuery(id+"F3.opExtrude","CAP_FACE",FACE,{"disambiguationData":[OSD([sQuery(id+"F2.wireOp",EDGE,"E2.15.10.0")])],"isStart":false})}),makeQuery(id+"F3.boolean.opBoolean","COPY",FACE,{"derivedFrom":makeQuery(id+"F3.opExtrude","CAP_FACE",FACE,{"disambiguationData":[OSD([sQuery(id+"F2.wireOp",EDGE,"E2.15.11.0")])],"isStart":false})}),makeQuery(id+"F3.boolean.opBoolean","COPY",FACE,{"derivedFrom":makeQuery(id+"F3.opExtrude","CAP_FACE",FACE,{"disambiguationData":[OSD([sQuery(id+"F2.wireOp",EDGE,"E2.16.0.0")])],"isStart":false})}),makeQuery(id+"F3.boolean.opBoolean","COPY",FACE,{"derivedFrom":makeQuery(id+"F3.opExtrude","CAP_FACE",FACE,{"disambiguationData":[OSD([sQuery(id+"F2.wireOp",EDGE,"E2.16.1.0")])],"isStart":false})}),makeQuery(id+"F3.boolean.opBoolean","COPY",FACE,{"derivedFrom":makeQuery(id+"F3.opExtrude","CAP_FACE",FACE,{"disambiguationData":[OSD([sQuery(id+"F2.wireOp",EDGE,"E2.16.2.0")])],"isStart":false})}),makeQuery(id+"F3.boolean.opBoolean","COPY",FACE,{"derivedFrom":makeQuery(id+"F3.opExtrude","CAP_FACE",FACE,{"disambiguationData":[OSD([sQuery(id+"F2.wireOp",EDGE,"E2.16.3.0")])],"isStart":false})}),makeQuery(id+"F3.boolean.opBoolean","COPY",FACE,{"derivedFrom":makeQuery(id+"F3.opExtrude","CAP_FACE",FACE,{"disambiguationData":[OSD([sQuery(id+"F2.wireOp",EDGE,"E2.16.4.0")])],"isStart":false})}),makeQuery(id+"F3.boolean.opBoolean","COPY",FACE,{"derivedFrom":makeQuery(id+"F3.opExtrude","CAP_FACE",FACE,{"disambiguationData":[OSD([sQuery(id+"F2.wireOp",EDGE,"E2.16.5.0")])],"isStart":false})}),makeQuery(id+"F3.boolean.opBoolean","COPY",FACE,{"derivedFrom":makeQuery(id+"F3.opExtrude","CAP_FACE",FACE,{"disambiguationData":[OSD([sQuery(id+"F2.wireOp",EDGE,"E2.16.6.0")])],"isStart":false})}),makeQuery(id+"F3.boolean.opBoolean","COPY",FACE,{"derivedFrom":makeQuery(id+"F3.opExtrude","CAP_FACE",FACE,{"disambiguationData":[OSD([sQuery(id+"F2.wireOp",EDGE,"E2.16.7.0")])],"isStart":false})}),makeQuery(id+"F3.boolean.opBoolean","COPY",FACE,{"derivedFrom":makeQuery(id+"F3.opExtrude","CAP_FACE",FACE,{"disambiguationData":[OSD([sQuery(id+"F2.wireOp",EDGE,"E2.16.8.0")])],"isStart":false})}),makeQuery(id+"F3.boolean.opBoolean","COPY",FACE,{"derivedFrom":makeQuery(id+"F3.opExtrude","CAP_FACE",FACE,{"disambiguationData":[OSD([sQuery(id+"F2.wireOp",EDGE,"E2.16.9.0")])],"isStart":false})}),makeQuery(id+"F3.boolean.opBoolean","COPY",FACE,{"derivedFrom":makeQuery(id+"F3.opExtrude","CAP_FACE",FACE,{"disambiguationData":[OSD([sQuery(id+"F2.wireOp",EDGE,"E2.16.10.0")])],"isStart":false})}),makeQuery(id+"F3.boolean.opBoolean","COPY",FACE,{"derivedFrom":makeQuery(id+"F3.opExtrude","CAP_FACE",FACE,{"disambiguationData":[OSD([sQuery(id+"F2.wireOp",EDGE,"E2.16.11.0")])],"isStart":false})}),makeQuery(id+"F3.boolean.opBoolean","COPY",FACE,{"derivedFrom":makeQuery(id+"F3.opExtrude","CAP_FACE",FACE,{"disambiguationData":[OSD([sQuery(id+"F2.wireOp",EDGE,"E2.17.0.0")])],"isStart":false})}),makeQuery(id+"F3.boolean.opBoolean","COPY",FACE,{"derivedFrom":makeQuery(id+"F3.opExtrude","CAP_FACE",FACE,{"disambiguationData":[OSD([sQuery(id+"F2.wireOp",EDGE,"E2.17.1.0")])],"isStart":false})}),makeQuery(id+"F3.boolean.opBoolean","COPY",FACE,{"derivedFrom":makeQuery(id+"F3.opExtrude","CAP_FACE",FACE,{"disambiguationData":[OSD([sQuery(id+"F2.wireOp",EDGE,"E2.17.2.0")])],"isStart":false})}),makeQuery(id+"F3.boolean.opBoolean","COPY",FACE,{"derivedFrom":makeQuery(id+"F3.opExtrude","CAP_FACE",FACE,{"disambiguationData":[OSD([sQuery(id+"F2.wireOp",EDGE,"E2.17.3.0")])],"isStart":false})}),makeQuery(id+"F3.boolean.opBoolean","COPY",FACE,{"derivedFrom":makeQuery(id+"F3.opExtrude","CAP_FACE",FACE,{"disambiguationData":[OSD([sQuery(id+"F2.wireOp",EDGE,"E2.17.4.0")])],"isStart":false})}),makeQuery(id+"F3.boolean.opBoolean","COPY",FACE,{"derivedFrom":makeQuery(id+"F3.opExtrude","CAP_FACE",FACE,{"disambiguationData":[OSD([sQuery(id+"F2.wireOp",EDGE,"E2.17.5.0")])],"isStart":false})}),makeQuery(id+"F3.boolean.opBoolean","COPY",FACE,{"derivedFrom":makeQuery(id+"F3.opExtrude","CAP_FACE",FACE,{"disambiguationData":[OSD([sQuery(id+"F2.wireOp",EDGE,"E2.17.6.0")])],"isStart":false})}),makeQuery(id+"F3.boolean.opBoolean","COPY",FACE,{"derivedFrom":makeQuery(id+"F3.opExtrude","CAP_FACE",FACE,{"disambiguationData":[OSD([sQuery(id+"F2.wireOp",EDGE,"E2.17.7.0")])],"isStart":false})}),makeQuery(id+"F3.boolean.opBoolean","COPY",FACE,{"derivedFrom":makeQuery(id+"F3.opExtrude","CAP_FACE",FACE,{"disambiguationData":[OSD([sQuery(id+"F2.wireOp",EDGE,"E2.17.8.0")])],"isStart":false})}),makeQuery(id+"F3.boolean.opBoolean","COPY",FACE,{"derivedFrom":makeQuery(id+"F3.opExtrude","CAP_FACE",FACE,{"disambiguationData":[OSD([sQuery(id+"F2.wireOp",EDGE,"E2.17.9.0")])],"isStart":false})}),makeQuery(id+"F3.boolean.opBoolean","COPY",FACE,{"derivedFrom":makeQuery(id+"F3.opExtrude","CAP_FACE",FACE,{"disambiguationData":[OSD([sQuery(id+"F2.wireOp",EDGE,"E2.17.10.0")])],"isStart":false})}),makeQuery(id+"F3.boolean.opBoolean","COPY",FACE,{"derivedFrom":makeQuery(id+"F3.opExtrude","CAP_FACE",FACE,{"disambiguationData":[OSD([sQuery(id+"F2.wireOp",EDGE,"E2.17.11.0")])],"isStart":false})}),makeQuery(id+"F3.boolean.opBoolean","COPY",FACE,{"derivedFrom":makeQuery(id+"F3.opExtrude","CAP_FACE",FACE,{"disambiguationData":[OSD([sQuery(id+"F2.wireOp",EDGE,"E2.18.0.0")])],"isStart":false})}),makeQuery(id+"F3.boolean.opBoolean","COPY",FACE,{"derivedFrom":makeQuery(id+"F3.opExtrude","CAP_FACE",FACE,{"disambiguationData":[OSD([sQuery(id+"F2.wireOp",EDGE,"E2.18.1.0")])],"isStart":false})}),makeQuery(id+"F3.boolean.opBoolean","COPY",FACE,{"derivedFrom":makeQuery(id+"F3.opExtrude","CAP_FACE",FACE,{"disambiguationData":[OSD([sQuery(id+"F2.wireOp",EDGE,"E2.18.2.0")])],"isStart":false})}),makeQuery(id+"F3.boolean.opBoolean","COPY",FACE,{"derivedFrom":makeQuery(id+"F3.opExtrude","CAP_FACE",FACE,{"disambiguationData":[OSD([sQuery(id+"F2.wireOp",EDGE,"E2.18.3.0")])],"isStart":false})}),makeQuery(id+"F3.boolean.opBoolean","COPY",FACE,{"derivedFrom":makeQuery(id+"F3.opExtrude","CAP_FACE",FACE,{"disambiguationData":[OSD([sQuery(id+"F2.wireOp",EDGE,"E2.18.4.0")])],"isStart":false})}),makeQuery(id+"F3.boolean.opBoolean","COPY",FACE,{"derivedFrom":makeQuery(id+"F3.opExtrude","CAP_FACE",FACE,{"disambiguationData":[OSD([sQuery(id+"F2.wireOp",EDGE,"E2.18.5.0")])],"isStart":false})}),makeQuery(id+"F3.boolean.opBoolean","COPY",FACE,{"derivedFrom":makeQuery(id+"F3.opExtrude","CAP_FACE",FACE,{"disambiguationData":[OSD([sQuery(id+"F2.wireOp",EDGE,"E2.18.6.0")])],"isStart":false})}),makeQuery(id+"F3.boolean.opBoolean","COPY",FACE,{"derivedFrom":makeQuery(id+"F3.opExtrude","CAP_FACE",FACE,{"disambiguationData":[OSD([sQuery(id+"F2.wireOp",EDGE,"E2.18.7.0")])],"isStart":false})}),makeQuery(id+"F3.boolean.opBoolean","COPY",FACE,{"derivedFrom":makeQuery(id+"F3.opExtrude","CAP_FACE",FACE,{"disambiguationData":[OSD([sQuery(id+"F2.wireOp",EDGE,"E2.18.8.0")])],"isStart":false})}),makeQuery(id+"F3.boolean.opBoolean","COPY",FACE,{"derivedFrom":makeQuery(id+"F3.opExtrude","CAP_FACE",FACE,{"disambiguationData":[OSD([sQuery(id+"F2.wireOp",EDGE,"E2.18.9.0")])],"isStart":false})}),makeQuery(id+"F3.boolean.opBoolean","COPY",FACE,{"derivedFrom":makeQuery(id+"F3.opExtrude","CAP_FACE",FACE,{"disambiguationData":[OSD([sQuery(id+"F2.wireOp",EDGE,"E2.18.10.0")])],"isStart":false})}),makeQuery(id+"F3.boolean.opBoolean","COPY",FACE,{"derivedFrom":makeQuery(id+"F3.opExtrude","CAP_FACE",FACE,{"disambiguationData":[OSD([sQuery(id+"F2.wireOp",EDGE,"E2.18.11.0")])],"isStart":false})}),makeQuery(id+"F8.opExtrude","CAP_FACE",FACE,{"disambiguationData":[OSD([sQuery(id+"F7.wireOp",EDGE,"E6.bottom"),sQuery(id+"F7.wireOp",EDGE,"E6.top"),sQuery(id+"F7.wireOp",EDGE,"E6.left"),sQuery(id+"F7.wireOp",EDGE,"E6.right")])],"isStart":false})]});
            var sketch = newSketch(context, id + "F9", { "sketchPlane" : qUnion([Q0])});
            skLineSegment(sketch, "E7.bottom", {"start": v(-17.78, 11.43) * mm, "end": v(17.78, 11.43) * mm});
            skLineSegment(sketch, "E7.top", {"start": v(-17.78, -11.43) * mm, "end": v(17.78, -11.43) * mm});
            skLineSegment(sketch, "E7.left", {"start": v(-17.78, 11.43) * mm, "end": v(-17.78, -11.43) * mm});
            skLineSegment(sketch, "E7.right", {"start": v(17.78, 11.43) * mm, "end": v(17.78, -11.43) * mm});
            skSolve(sketch);
        }
        {
            var Q0;
            Q0=qSketchRegion(id+"F9",true);
            extrude(context, id + "F10", {"entities" : qUnion([Q0]), "operationType" : NewBodyOperationType.REMOVE, "oppositeDirection" : true, "depth" : 25.4 * mm, "offsetDistance" : 25.4 * mm});
        }
    });
